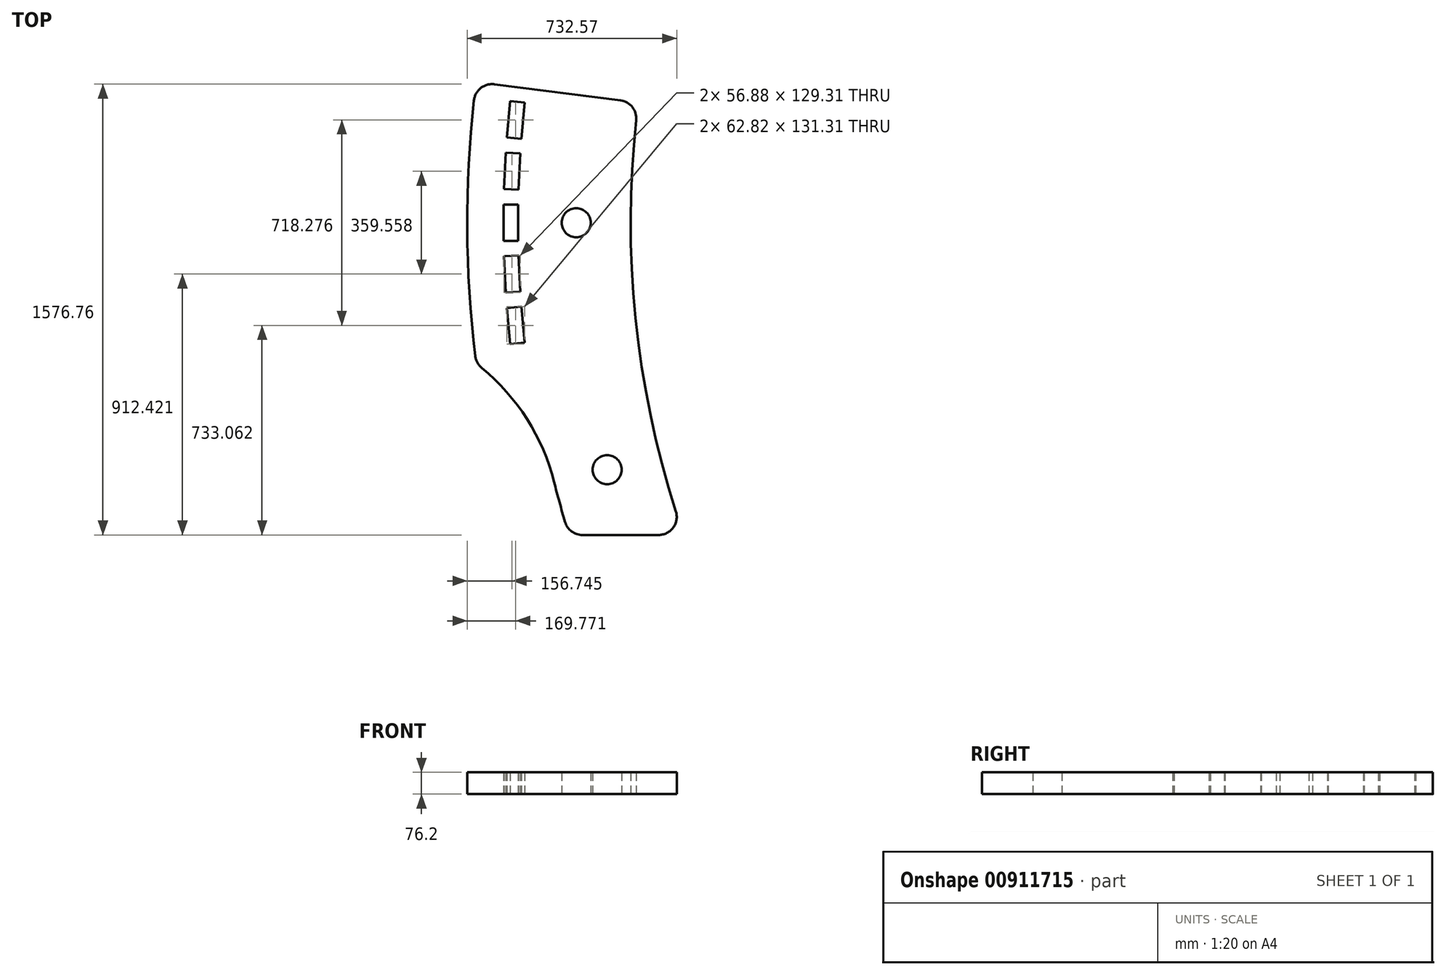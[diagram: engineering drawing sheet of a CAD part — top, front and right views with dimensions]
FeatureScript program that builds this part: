
annotation { "Feature Type Name" : "Feature", "Feature Type Description" : "" }
export const myFeature = defineFeature(function(context is Context, id is Id, definition is map)
    precondition{}
    {
        {
            var Q0;
            Q0=qCreatedBy(makeId("Top.planeOp"),FACE);
            var sketch = newSketch(context, id + "F0", { "sketchPlane" : qUnion([Q0])});
            skLineSegment(sketch, "E0.bottom", {"start": v(-635, -635) * mm, "end": v(635, -635) * mm, "construction": true});
            skLineSegment(sketch, "E0.top", {"start": v(-635, 635) * mm, "end": v(635, 635) * mm, "construction": true});
            skLineSegment(sketch, "E0.left", {"start": v(-635, -635) * mm, "end": v(-635, 635) * mm, "construction": true});
            skLineSegment(sketch, "E0.right", {"start": v(635, -635) * mm, "end": v(635, 635) * mm, "construction": true});
            skPoint(sketch, "E0.middle", {"position": v(0, 0) * mm});
            skPoint(sketch, "E1", {"position": v(0, -635) * mm});
            skLineSegment(sketch, "E2", {"start": v(2487.91, -1226.43) * mm, "end": v(2553.25, -1226.43) * mm});
            skLineSegment(sketch, "E3", {"start": v(2553.25, -1226.43) * mm, "end": v(2589.47, -1126.9) * mm});
            skLineSegment(sketch, "E4", {"start": v(2284.75, -1226.43) * mm, "end": v(2349.36, -1226.43) * mm});
            skLineSegment(sketch, "E5", {"start": v(2349.36, -1226.43) * mm, "end": v(2385.58, -1126.9) * mm});
            skLineSegment(sketch, "E6", {"start": v(2385.58, -1126.9) * mm, "end": v(2451.69, -1126.9) * mm});
            skLineSegment(sketch, "E7", {"start": v(2451.69, -1126.9) * mm, "end": v(2487.91, -1226.43) * mm});
            skLineSegment(sketch, "E8", {"start": v(2081.59, -1226.43) * mm, "end": v(2146.2, -1226.43) * mm});
            skLineSegment(sketch, "E9", {"start": v(2146.2, -1226.43) * mm, "end": v(2182.42, -1126.9) * mm});
            skLineSegment(sketch, "E10", {"start": v(2182.42, -1126.9) * mm, "end": v(2248.52, -1126.9) * mm});
            skLineSegment(sketch, "E11", {"start": v(2248.52, -1126.9) * mm, "end": v(2284.75, -1226.43) * mm});
            skLineSegment(sketch, "E12", {"start": v(1878.43, -1226.43) * mm, "end": v(1943.03, -1226.43) * mm});
            skLineSegment(sketch, "E13", {"start": v(1943.03, -1226.43) * mm, "end": v(1979.26, -1126.9) * mm});
            skLineSegment(sketch, "E14", {"start": v(1979.26, -1126.9) * mm, "end": v(2045.36, -1126.9) * mm});
            skLineSegment(sketch, "E15", {"start": v(2045.36, -1126.9) * mm, "end": v(2081.59, -1226.43) * mm});
            skLineSegment(sketch, "E16", {"start": v(1675.26, -1226.43) * mm, "end": v(1739.87, -1226.43) * mm});
            skLineSegment(sketch, "E17", {"start": v(1739.87, -1226.43) * mm, "end": v(1776.1, -1126.9) * mm});
            skLineSegment(sketch, "E18", {"start": v(1776.1, -1126.9) * mm, "end": v(1842.2, -1126.9) * mm});
            skLineSegment(sketch, "E19", {"start": v(1842.2, -1126.9) * mm, "end": v(1878.43, -1226.43) * mm});
            skLineSegment(sketch, "E20", {"start": v(1472.1, -1226.43) * mm, "end": v(1536.71, -1226.43) * mm});
            skLineSegment(sketch, "E21", {"start": v(1536.71, -1226.43) * mm, "end": v(1572.94, -1126.9) * mm});
            skLineSegment(sketch, "E22", {"start": v(1572.94, -1126.9) * mm, "end": v(1639.04, -1126.9) * mm});
            skLineSegment(sketch, "E23", {"start": v(1639.04, -1126.9) * mm, "end": v(1675.26, -1226.43) * mm});
            skLineSegment(sketch, "E24", {"start": v(1268.94, -1226.43) * mm, "end": v(1333.55, -1226.43) * mm});
            skLineSegment(sketch, "E25", {"start": v(1333.55, -1226.43) * mm, "end": v(1369.77, -1126.9) * mm});
            skLineSegment(sketch, "E26", {"start": v(1369.77, -1126.9) * mm, "end": v(1435.88, -1126.9) * mm});
            skLineSegment(sketch, "E27", {"start": v(1435.88, -1126.9) * mm, "end": v(1472.1, -1226.43) * mm});
            skLineSegment(sketch, "E28", {"start": v(1065.78, -1226.43) * mm, "end": v(1130.39, -1226.43) * mm});
            skLineSegment(sketch, "E29", {"start": v(1130.39, -1226.43) * mm, "end": v(1166.61, -1126.9) * mm});
            skLineSegment(sketch, "E30", {"start": v(1166.61, -1126.9) * mm, "end": v(1232.71, -1126.9) * mm});
            skLineSegment(sketch, "E31", {"start": v(1232.71, -1126.9) * mm, "end": v(1268.94, -1226.43) * mm});
            skLineSegment(sketch, "E32", {"start": v(862.62, -1226.43) * mm, "end": v(927.23, -1226.43) * mm});
            skLineSegment(sketch, "E33", {"start": v(927.23, -1226.43) * mm, "end": v(963.45, -1126.9) * mm});
            skLineSegment(sketch, "E34", {"start": v(963.45, -1126.9) * mm, "end": v(1029.55, -1126.9) * mm});
            skLineSegment(sketch, "E35", {"start": v(1029.55, -1126.9) * mm, "end": v(1065.78, -1226.43) * mm});
            skLineSegment(sketch, "E36", {"start": v(659.45, -1226.43) * mm, "end": v(724.06, -1226.43) * mm});
            skLineSegment(sketch, "E37", {"start": v(724.06, -1226.43) * mm, "end": v(760.29, -1126.9) * mm});
            skLineSegment(sketch, "E38", {"start": v(760.29, -1126.9) * mm, "end": v(826.4, -1126.9) * mm});
            skLineSegment(sketch, "E39", {"start": v(826.4, -1126.9) * mm, "end": v(862.62, -1226.43) * mm});
            skLineSegment(sketch, "E40", {"start": v(456.3, -1226.43) * mm, "end": v(520.9, -1226.43) * mm});
            skLineSegment(sketch, "E41", {"start": v(520.9, -1226.43) * mm, "end": v(557.13, -1126.9) * mm});
            skLineSegment(sketch, "E42", {"start": v(557.13, -1126.9) * mm, "end": v(623.23, -1126.9) * mm});
            skLineSegment(sketch, "E43", {"start": v(623.23, -1126.9) * mm, "end": v(659.45, -1226.43) * mm});
            skLineSegment(sketch, "E44", {"start": v(253.13, -1226.43) * mm, "end": v(317.74, -1226.43) * mm});
            skLineSegment(sketch, "E45", {"start": v(317.74, -1226.43) * mm, "end": v(353.97, -1126.9) * mm});
            skLineSegment(sketch, "E46", {"start": v(353.97, -1126.9) * mm, "end": v(420.07, -1126.9) * mm});
            skLineSegment(sketch, "E47", {"start": v(420.07, -1126.9) * mm, "end": v(456.3, -1226.43) * mm});
            skLineSegment(sketch, "E48", {"start": v(49.97, -1226.43) * mm, "end": v(114.58, -1226.43) * mm});
            skLineSegment(sketch, "E49", {"start": v(114.58, -1226.43) * mm, "end": v(150.8, -1126.9) * mm});
            skLineSegment(sketch, "E50", {"start": v(150.8, -1126.9) * mm, "end": v(216.9, -1126.9) * mm});
            skLineSegment(sketch, "E51", {"start": v(216.9, -1126.9) * mm, "end": v(253.13, -1226.43) * mm});
            skLineSegment(sketch, "E52", {"start": v(-153.2, -1226.43) * mm, "end": v(-88.58, -1226.43) * mm});
            skLineSegment(sketch, "E53", {"start": v(-88.58, -1226.43) * mm, "end": v(-52.36, -1126.9) * mm});
            skLineSegment(sketch, "E54", {"start": v(-52.36, -1126.9) * mm, "end": v(13.74, -1126.9) * mm});
            skLineSegment(sketch, "E55", {"start": v(13.74, -1126.9) * mm, "end": v(49.97, -1226.43) * mm});
            skLineSegment(sketch, "E56", {"start": v(-356.35, -1226.43) * mm, "end": v(-291.75, -1226.43) * mm});
            skLineSegment(sketch, "E57", {"start": v(-291.75, -1226.43) * mm, "end": v(-255.52, -1126.9) * mm});
            skLineSegment(sketch, "E58", {"start": v(-255.52, -1126.9) * mm, "end": v(-189.42, -1126.9) * mm});
            skLineSegment(sketch, "E59", {"start": v(-189.42, -1126.9) * mm, "end": v(-153.2, -1226.43) * mm});
            skLineSegment(sketch, "E60", {"start": v(-559.52, -1226.43) * mm, "end": v(-494.9, -1226.43) * mm});
            skLineSegment(sketch, "E61", {"start": v(-494.9, -1226.43) * mm, "end": v(-458.68, -1126.9) * mm});
            skLineSegment(sketch, "E62", {"start": v(-458.68, -1126.9) * mm, "end": v(-392.58, -1126.9) * mm});
            skLineSegment(sketch, "E63", {"start": v(-392.58, -1126.9) * mm, "end": v(-356.35, -1226.43) * mm});
            skLineSegment(sketch, "E64", {"start": v(-762.68, -1226.43) * mm, "end": v(-698.07, -1226.43) * mm});
            skLineSegment(sketch, "E65", {"start": v(-698.07, -1226.43) * mm, "end": v(-661.84, -1126.9) * mm});
            skLineSegment(sketch, "E66", {"start": v(-661.84, -1126.9) * mm, "end": v(-595.74, -1126.9) * mm});
            skLineSegment(sketch, "E67", {"start": v(-595.74, -1126.9) * mm, "end": v(-559.52, -1226.43) * mm});
            skLineSegment(sketch, "E68", {"start": v(-965.84, -1226.43) * mm, "end": v(-901.23, -1226.43) * mm});
            skLineSegment(sketch, "E69", {"start": v(-901.23, -1226.43) * mm, "end": v(-865, -1126.9) * mm});
            skLineSegment(sketch, "E70", {"start": v(-865, -1126.9) * mm, "end": v(-798.9, -1126.9) * mm});
            skLineSegment(sketch, "E71", {"start": v(-798.9, -1126.9) * mm, "end": v(-762.68, -1226.43) * mm});
            skLineSegment(sketch, "E72", {"start": v(-1169, -1226.43) * mm, "end": v(-1104.4, -1226.43) * mm});
            skLineSegment(sketch, "E73", {"start": v(-1104.4, -1226.43) * mm, "end": v(-1068.17, -1126.9) * mm});
            skLineSegment(sketch, "E74", {"start": v(-1068.17, -1126.9) * mm, "end": v(-1002.06, -1126.9) * mm});
            skLineSegment(sketch, "E75", {"start": v(-1002.06, -1126.9) * mm, "end": v(-965.84, -1226.43) * mm});
            skLineSegment(sketch, "E76", {"start": v(-1372.16, -1226.43) * mm, "end": v(-1307.55, -1226.43) * mm});
            skLineSegment(sketch, "E77", {"start": v(-1307.55, -1226.43) * mm, "end": v(-1271.33, -1126.9) * mm});
            skLineSegment(sketch, "E78", {"start": v(-1271.33, -1126.9) * mm, "end": v(-1205.23, -1126.9) * mm});
            skLineSegment(sketch, "E79", {"start": v(-1205.23, -1126.9) * mm, "end": v(-1169, -1226.43) * mm});
            skLineSegment(sketch, "E80", {"start": v(-1575.32, -1226.43) * mm, "end": v(-1510.72, -1226.43) * mm});
            skLineSegment(sketch, "E81", {"start": v(-1510.72, -1226.43) * mm, "end": v(-1474.5, -1126.9) * mm});
            skLineSegment(sketch, "E82", {"start": v(-1474.5, -1126.9) * mm, "end": v(-1408.39, -1126.9) * mm});
            skLineSegment(sketch, "E83", {"start": v(-1408.39, -1126.9) * mm, "end": v(-1372.16, -1226.43) * mm});
            skLineSegment(sketch, "E84", {"start": v(-1778.49, -1226.43) * mm, "end": v(-1713.88, -1226.43) * mm});
            skLineSegment(sketch, "E85", {"start": v(-1713.88, -1226.43) * mm, "end": v(-1677.65, -1126.9) * mm});
            skLineSegment(sketch, "E86", {"start": v(-1677.65, -1126.9) * mm, "end": v(-1611.55, -1126.9) * mm});
            skLineSegment(sketch, "E87", {"start": v(-1611.55, -1126.9) * mm, "end": v(-1575.32, -1226.43) * mm});
            skLineSegment(sketch, "E88", {"start": v(-1981.65, -1226.43) * mm, "end": v(-1917.04, -1226.43) * mm});
            skLineSegment(sketch, "E89", {"start": v(-1917.04, -1226.43) * mm, "end": v(-1880.81, -1126.9) * mm});
            skLineSegment(sketch, "E90", {"start": v(-1880.81, -1126.9) * mm, "end": v(-1814.71, -1126.9) * mm});
            skLineSegment(sketch, "E91", {"start": v(-1814.71, -1126.9) * mm, "end": v(-1778.49, -1226.43) * mm});
            skLineSegment(sketch, "E92", {"start": v(-2184.8, -1226.43) * mm, "end": v(-2120.2, -1226.43) * mm});
            skLineSegment(sketch, "E93", {"start": v(-2120.2, -1226.43) * mm, "end": v(-2083.98, -1126.9) * mm});
            skLineSegment(sketch, "E94", {"start": v(-2083.98, -1126.9) * mm, "end": v(-2017.87, -1126.9) * mm});
            skLineSegment(sketch, "E95", {"start": v(-2017.87, -1126.9) * mm, "end": v(-1981.65, -1226.43) * mm});
            skLineSegment(sketch, "E96", {"start": v(-2388.2, -1226.43) * mm, "end": v(-2323.36, -1226.43) * mm});
            skLineSegment(sketch, "E97", {"start": v(-2323.36, -1226.43) * mm, "end": v(-2287.14, -1126.9) * mm});
            skLineSegment(sketch, "E98", {"start": v(-2287.14, -1126.9) * mm, "end": v(-2221.04, -1126.9) * mm});
            skLineSegment(sketch, "E99", {"start": v(-2221.04, -1126.9) * mm, "end": v(-2184.8, -1226.43) * mm});
            skLineSegment(sketch, "E100", {"start": v(-2491.46, -1126.9) * mm, "end": v(-2424.43, -1126.9) * mm});
            skLineSegment(sketch, "E101", {"start": v(-2424.43, -1126.9) * mm, "end": v(-2388.2, -1226.43) * mm});
            skCircle(sketch, "E102", {"center": v(-3384.04, -863.6) * mm, "radius": 50.8 * mm});
            skLineSegment(sketch, "E103", {"start": v(-2592.51, -1226.47) * mm, "end": v(-2527.69, -1226.43) * mm});
            skLineSegment(sketch, "E104", {"start": v(-2527.69, -1226.43) * mm, "end": v(-2491.46, -1126.9) * mm});
            skLineSegment(sketch, "E105", {"start": v(-2629.3, -1126.9) * mm, "end": v(-2592.51, -1226.47) * mm});
            skLineSegment(sketch, "E106", {"start": v(-2696.33, -1126.9) * mm, "end": v(-2629.3, -1126.9) * mm});
            skLineSegment(sketch, "E107", {"start": v(-2733.1, -1226.43) * mm, "end": v(-2696.33, -1126.9) * mm});
            skLineSegment(sketch, "E108", {"start": v(2691.8, -1226.43) * mm, "end": v(2757.13, -1226.43) * mm});
            skLineSegment(sketch, "E109", {"start": v(2757.13, -1226.43) * mm, "end": v(2794, -1126.75) * mm});
            skLineSegment(sketch, "E110", {"start": v(2589.47, -1126.9) * mm, "end": v(2655.57, -1126.9) * mm});
            skLineSegment(sketch, "E111", {"start": v(2655.57, -1126.9) * mm, "end": v(2691.8, -1226.43) * mm});
            skLineSegment(sketch, "E112", {"start": v(-2794.02, -1226.47) * mm, "end": v(-2733.1, -1226.43) * mm});
            skCircle(sketch, "E113", {"center": v(-2980.94, -863.6) * mm, "radius": 76.2 * mm});
            skCircle(sketch, "E114", {"center": v(3463.58, -863.6) * mm, "radius": 76.2 * mm});
            skLineSegment(sketch, "E115", {"start": v(-2980.94, -787.4) * mm, "end": v(3463.58, -787.4) * mm});
            skLineSegment(sketch, "E116", {"start": v(3463.58, -939.8) * mm, "end": v(-2980.94, -939.8) * mm});
            skLineSegment(sketch, "E117.bottom", {"start": v(-2794, -635) * mm, "end": v(2794, -635) * mm});
            skLineSegment(sketch, "E117.top", {"start": v(-2794, -1176.6) * mm, "end": v(3692.18, -1176.6) * mm, "construction": true});
            skLineSegment(sketch, "E117.left", {"start": v(-2794, -635) * mm, "end": v(-2794, -1176.6) * mm});
            skLineSegment(sketch, "E118", {"start": v(-2794.02, -1226.47) * mm, "end": v(-2794, -1176.6) * mm});
            skLineSegment(sketch, "E119.bottom", {"start": v(-2794, -635) * mm, "end": v(-4256.94, -635) * mm});
            skLineSegment(sketch, "E119.top", {"start": v(-2794, -1092.2) * mm, "end": v(-4256.94, -1092.2) * mm});
            skLineSegment(sketch, "E119.left", {"start": v(-2794, -635) * mm, "end": v(-2794, -1092.2) * mm});
            skLineSegment(sketch, "E119.right", {"start": v(-4256.94, -635) * mm, "end": v(-4256.94, -1092.2) * mm});
            skLineSegment(sketch, "E120.bottom", {"start": v(2794, -635) * mm, "end": v(3692.18, -635) * mm});
            skLineSegment(sketch, "E120.right", {"start": v(3692.18, -635) * mm, "end": v(3692.18, -1238.28) * mm});
            skPoint(sketch, "E121", {"position": v(-3803.14, -635) * mm});
            skPoint(sketch, "E122", {"position": v(3237.88, -635) * mm});
            skLineSegment(sketch, "E123", {"start": v(2896.33, -1226.28) * mm, "end": v(2961.66, -1226.28) * mm});
            skLineSegment(sketch, "E124", {"start": v(2961.66, -1226.28) * mm, "end": v(2998.53, -1126.6) * mm});
            skLineSegment(sketch, "E125", {"start": v(2794, -1126.75) * mm, "end": v(2860.1, -1126.75) * mm});
            skLineSegment(sketch, "E126", {"start": v(2860.1, -1126.75) * mm, "end": v(2896.33, -1226.28) * mm});
            skLineSegment(sketch, "E127", {"start": v(3100.86, -1226.14) * mm, "end": v(3166.2, -1226.14) * mm});
            skLineSegment(sketch, "E128", {"start": v(3166.2, -1226.14) * mm, "end": v(3203.06, -1126.46) * mm});
            skLineSegment(sketch, "E129", {"start": v(2998.53, -1126.6) * mm, "end": v(3064.63, -1126.6) * mm});
            skLineSegment(sketch, "E130", {"start": v(3064.63, -1126.6) * mm, "end": v(3100.86, -1226.14) * mm});
            skLineSegment(sketch, "E131", {"start": v(3305.39, -1226) * mm, "end": v(3370.72, -1226) * mm});
            skLineSegment(sketch, "E132", {"start": v(3370.72, -1226) * mm, "end": v(3407.59, -1126.32) * mm});
            skLineSegment(sketch, "E133", {"start": v(3203.06, -1126.46) * mm, "end": v(3269.16, -1126.46) * mm});
            skLineSegment(sketch, "E134", {"start": v(3269.16, -1126.46) * mm, "end": v(3305.39, -1226) * mm});
            skLineSegment(sketch, "E135", {"start": v(3509.7, -1226.43) * mm, "end": v(3575.03, -1226.43) * mm});
            skLineSegment(sketch, "E136", {"start": v(3575.03, -1226.43) * mm, "end": v(3611.9, -1126.75) * mm});
            skLineSegment(sketch, "E137", {"start": v(3407.37, -1126.9) * mm, "end": v(3473.47, -1126.9) * mm});
            skLineSegment(sketch, "E138", {"start": v(3473.47, -1126.9) * mm, "end": v(3509.7, -1226.43) * mm});
            skLineSegment(sketch, "E139", {"start": v(3611.9, -1126.75) * mm, "end": v(3692.18, -1126.75) * mm});
            skPoint(sketch, "E140", {"position": v(3692.18, -1176.6) * mm});
            skPoint(sketch, "E140.positionSnap0", {"position": v(3593.47, -1176.6) * mm});
            skLineSegment(sketch, "E141.bottom", {"start": v(-3107.94, -635) * mm, "end": v(-2853.94, -635) * mm});
            skLineSegment(sketch, "E141.top", {"start": v(-3107.94, -254) * mm, "end": v(-2853.94, -254) * mm});
            skLineSegment(sketch, "E141.left", {"start": v(-3107.94, -635) * mm, "end": v(-3107.94, -254) * mm});
            skLineSegment(sketch, "E141.right", {"start": v(-2853.94, -635) * mm, "end": v(-2853.94, -254) * mm});
            skPoint(sketch, "E142", {"position": v(-2980.94, -635) * mm});
            skCircle(sketch, "E143", {"center": v(0, 0) * mm, "radius": 3302 * mm});
            skCircle(sketch, "E144", {"center": v(0, 0) * mm, "radius": 3683 * mm});
            skCircle(sketch, "E145", {"center": v(0, 0) * mm, "radius": 3492.5 * mm, "construction": true});
            skLineSegment(sketch, "E146", {"start": v(-2980.94, -863.6) * mm, "end": v(-3692.14, -863.6) * mm, "construction": true});
            skLineSegment(sketch, "E147", {"start": v(0, 0) * mm, "end": v(-3873.5, 0) * mm, "construction": true});
            skCircle(sketch, "E148", {"center": v(-3492.5, 0) * mm, "radius": 50.8 * mm});
            skLineSegment(sketch, "E149", {"start": v(0, 0) * mm, "end": v(-3842.1, 492.18) * mm});
            skCircle(sketch, "E150", {"center": v(0, 0) * mm, "radius": 3873.5 * mm});
            skLineSegment(sketch, "E151.bottom", {"start": v(-3746.5, -63.5) * mm, "end": v(-3695.7, -63.5) * mm});
            skLineSegment(sketch, "E151.top", {"start": v(-3746.5, 63.5) * mm, "end": v(-3695.7, 63.5) * mm});
            skLineSegment(sketch, "E151.left", {"start": v(-3746.5, -63.5) * mm, "end": v(-3746.5, 63.5) * mm});
            skLineSegment(sketch, "E151.right", {"start": v(-3695.7, -63.5) * mm, "end": v(-3695.7, 63.5) * mm});
            skPoint(sketch, "E151.middle", {"position": v(-3721.1, 0) * mm});
            skLineSegment(sketch, "E152.1.0", {"start": v(-3739.06, -244.43) * mm, "end": v(-3688.32, -241.98) * mm});
            skLineSegment(sketch, "E152.1.1", {"start": v(-3688.32, -241.98) * mm, "end": v(-3694.45, -115.13) * mm});
            skLineSegment(sketch, "E152.1.2", {"start": v(-3745.2, -117.58) * mm, "end": v(-3694.45, -115.13) * mm});
            skLineSegment(sketch, "E152.1.3", {"start": v(-3739.06, -244.43) * mm, "end": v(-3745.2, -117.58) * mm});
            skLineSegment(sketch, "E152.2.0", {"start": v(-3722.88, -424.8) * mm, "end": v(-3672.32, -419.9) * mm});
            skLineSegment(sketch, "E152.2.1", {"start": v(-3672.32, -419.9) * mm, "end": v(-3684.58, -293.48) * mm});
            skLineSegment(sketch, "E152.2.2", {"start": v(-3735.14, -298.39) * mm, "end": v(-3684.58, -293.48) * mm});
            skLineSegment(sketch, "E152.2.3", {"start": v(-3722.88, -424.8) * mm, "end": v(-3735.14, -298.39) * mm});
            skLineSegment(sketch, "E152.3.0", {"start": v(-3698.01, -604.16) * mm, "end": v(-3647.74, -596.82) * mm});
            skLineSegment(sketch, "E152.3.1", {"start": v(-3647.74, -596.82) * mm, "end": v(-3666.1, -471.15) * mm});
            skLineSegment(sketch, "E152.3.2", {"start": v(-3716.36, -478.5) * mm, "end": v(-3666.1, -471.15) * mm});
            skLineSegment(sketch, "E152.3.3", {"start": v(-3698.01, -604.16) * mm, "end": v(-3716.36, -478.5) * mm});
            skLineSegment(sketch, "E152.4.0", {"start": v(-3664.5, -782.12) * mm, "end": v(-3614.65, -772.36) * mm});
            skLineSegment(sketch, "E152.4.1", {"start": v(-3614.65, -772.36) * mm, "end": v(-3639.05, -647.73) * mm});
            skLineSegment(sketch, "E152.4.2", {"start": v(-3688.9, -657.49) * mm, "end": v(-3639.05, -647.73) * mm});
            skLineSegment(sketch, "E152.4.3", {"start": v(-3664.5, -782.12) * mm, "end": v(-3688.9, -657.49) * mm});
            skLineSegment(sketch, "E152.5.0", {"start": v(-3622.44, -958.25) * mm, "end": v(-3573.11, -946.1) * mm});
            skLineSegment(sketch, "E152.5.1", {"start": v(-3573.11, -946.1) * mm, "end": v(-3603.5, -822.78) * mm});
            skLineSegment(sketch, "E152.5.2", {"start": v(-3652.83, -834.94) * mm, "end": v(-3603.5, -822.78) * mm});
            skLineSegment(sketch, "E152.5.3", {"start": v(-3622.44, -958.25) * mm, "end": v(-3652.83, -834.94) * mm});
            skLineSegment(sketch, "E152.6.0", {"start": v(-3571.91, -1132.14) * mm, "end": v(-3523.23, -1117.62) * mm});
            skLineSegment(sketch, "E152.6.1", {"start": v(-3523.23, -1117.62) * mm, "end": v(-3559.55, -995.92) * mm});
            skLineSegment(sketch, "E152.6.2", {"start": v(-3608.23, -1010.45) * mm, "end": v(-3559.55, -995.92) * mm});
            skLineSegment(sketch, "E152.6.3", {"start": v(-3571.91, -1132.14) * mm, "end": v(-3608.23, -1010.45) * mm});
            skLineSegment(sketch, "E152.7.0", {"start": v(-3513.04, -1303.4) * mm, "end": v(-3465.12, -1286.53) * mm});
            skLineSegment(sketch, "E152.7.1", {"start": v(-3465.12, -1286.53) * mm, "end": v(-3507.27, -1166.73) * mm});
            skLineSegment(sketch, "E152.7.2", {"start": v(-3555.2, -1183.6) * mm, "end": v(-3507.27, -1166.73) * mm});
            skLineSegment(sketch, "E152.7.3", {"start": v(-3513.04, -1303.4) * mm, "end": v(-3555.2, -1183.6) * mm});
            skLineSegment(sketch, "E152.8.0", {"start": v(-3445.97, -1471.6) * mm, "end": v(-3398.92, -1452.44) * mm});
            skLineSegment(sketch, "E152.8.1", {"start": v(-3398.92, -1452.44) * mm, "end": v(-3446.8, -1334.82) * mm});
            skLineSegment(sketch, "E152.8.2", {"start": v(-3493.86, -1353.97) * mm, "end": v(-3446.8, -1334.82) * mm});
            skLineSegment(sketch, "E152.8.3", {"start": v(-3445.97, -1471.6) * mm, "end": v(-3493.86, -1353.97) * mm});
            skLineSegment(sketch, "E152.9.0", {"start": v(-3370.85, -1636.37) * mm, "end": v(-3324.78, -1614.96) * mm});
            skLineSegment(sketch, "E152.9.1", {"start": v(-3324.78, -1614.96) * mm, "end": v(-3378.3, -1499.79) * mm});
            skLineSegment(sketch, "E152.9.2", {"start": v(-3424.36, -1521.2) * mm, "end": v(-3378.3, -1499.79) * mm});
            skLineSegment(sketch, "E152.9.3", {"start": v(-3370.85, -1636.37) * mm, "end": v(-3424.36, -1521.2) * mm});
            skLineSegment(sketch, "E152.10.0", {"start": v(-3287.85, -1797.31) * mm, "end": v(-3242.87, -1773.7) * mm});
            skLineSegment(sketch, "E152.10.1", {"start": v(-3242.87, -1773.7) * mm, "end": v(-3301.89, -1661.25) * mm});
            skLineSegment(sketch, "E152.10.2", {"start": v(-3346.87, -1684.86) * mm, "end": v(-3301.89, -1661.25) * mm});
            skLineSegment(sketch, "E152.10.3", {"start": v(-3287.85, -1797.31) * mm, "end": v(-3346.87, -1684.86) * mm});
            skLineSegment(sketch, "E152.11.0", {"start": v(-3197.18, -1954.06) * mm, "end": v(-3153.39, -1928.3) * mm});
            skLineSegment(sketch, "E152.11.1", {"start": v(-3153.39, -1928.3) * mm, "end": v(-3217.77, -1818.84) * mm});
            skLineSegment(sketch, "E152.11.2", {"start": v(-3261.56, -1844.6) * mm, "end": v(-3217.77, -1818.84) * mm});
            skLineSegment(sketch, "E152.11.3", {"start": v(-3197.18, -1954.06) * mm, "end": v(-3261.56, -1844.6) * mm});
            skLineSegment(sketch, "E152.12.0", {"start": v(-3099.04, -2106.24) * mm, "end": v(-3056.54, -2078.4) * mm});
            skLineSegment(sketch, "E152.12.1", {"start": v(-3056.54, -2078.4) * mm, "end": v(-3126.14, -1972.17) * mm});
            skLineSegment(sketch, "E152.12.2", {"start": v(-3168.63, -2000.01) * mm, "end": v(-3126.14, -1972.17) * mm});
            skLineSegment(sketch, "E152.12.3", {"start": v(-3099.04, -2106.24) * mm, "end": v(-3168.63, -2000.01) * mm});
            skLineSegment(sketch, "E153", {"start": v(0, 0) * mm, "end": v(-3842.1, -492.18) * mm});
            skLineSegment(sketch, "E154.1.13.0", {"start": v(-2993.66, -2253.51) * mm, "end": v(-2952.56, -2223.65) * mm});
            skLineSegment(sketch, "E154.3.13.0", {"start": v(-2952.56, -2223.65) * mm, "end": v(-3027.2, -2120.9) * mm});
            skLineSegment(sketch, "E154.6.13.0", {"start": v(-3068.3, -2150.76) * mm, "end": v(-3027.2, -2120.9) * mm});
            skLineSegment(sketch, "E154.9.13.0", {"start": v(-2993.66, -2253.51) * mm, "end": v(-3068.3, -2150.76) * mm});
            skLineSegment(sketch, "E154.1.14.0", {"start": v(-2881.29, -2395.51) * mm, "end": v(-2841.68, -2363.7) * mm});
            skLineSegment(sketch, "E154.3.14.0", {"start": v(-2841.68, -2363.7) * mm, "end": v(-2921.2, -2264.68) * mm});
            skLineSegment(sketch, "E154.6.14.0", {"start": v(-2960.81, -2296.5) * mm, "end": v(-2921.2, -2264.68) * mm});
            skLineSegment(sketch, "E154.9.14.0", {"start": v(-2881.29, -2395.51) * mm, "end": v(-2960.81, -2296.5) * mm});
            skLineSegment(sketch, "E154.1.15.0", {"start": v(-2762.19, -2531.92) * mm, "end": v(-2724.16, -2498.23) * mm});
            skLineSegment(sketch, "E154.3.15.0", {"start": v(-2724.16, -2498.23) * mm, "end": v(-2808.38, -2403.17) * mm});
            skLineSegment(sketch, "E154.6.15.0", {"start": v(-2846.4, -2436.86) * mm, "end": v(-2808.38, -2403.17) * mm});
            skLineSegment(sketch, "E154.9.15.0", {"start": v(-2762.19, -2531.92) * mm, "end": v(-2846.4, -2436.86) * mm});
            skLineSegment(sketch, "E154.1.16.0", {"start": v(-2636.64, -2662.41) * mm, "end": v(-2600.28, -2626.93) * mm});
            skLineSegment(sketch, "E154.3.16.0", {"start": v(-2600.28, -2626.93) * mm, "end": v(-2689, -2536.05) * mm});
            skLineSegment(sketch, "E154.6.16.0", {"start": v(-2725.35, -2571.53) * mm, "end": v(-2689, -2536.05) * mm});
            skLineSegment(sketch, "E154.9.16.0", {"start": v(-2636.64, -2662.41) * mm, "end": v(-2725.35, -2571.53) * mm});
            skLineSegment(sketch, "E154.1.17.0", {"start": v(-2504.93, -2786.69) * mm, "end": v(-2470.33, -2749.49) * mm});
            skLineSegment(sketch, "E154.3.17.0", {"start": v(-2470.33, -2749.49) * mm, "end": v(-2563.33, -2663) * mm});
            skLineSegment(sketch, "E154.6.17.0", {"start": v(-2597.92, -2700.2) * mm, "end": v(-2563.33, -2663) * mm});
            skLineSegment(sketch, "E154.9.17.0", {"start": v(-2504.93, -2786.69) * mm, "end": v(-2597.92, -2700.2) * mm});
            skLineSegment(sketch, "E154.1.18.0", {"start": v(-2367.37, -2904.46) * mm, "end": v(-2334.6, -2865.63) * mm});
            skLineSegment(sketch, "E154.3.18.0", {"start": v(-2334.6, -2865.63) * mm, "end": v(-2431.68, -2783.73) * mm});
            skLineSegment(sketch, "E154.6.18.0", {"start": v(-2464.44, -2822.56) * mm, "end": v(-2431.68, -2783.73) * mm});
            skLineSegment(sketch, "E154.9.18.0", {"start": v(-2367.37, -2904.46) * mm, "end": v(-2464.44, -2822.56) * mm});
            skLineSegment(sketch, "E154.1.19.0", {"start": v(-2224.28, -3015.44) * mm, "end": v(-2193.43, -2975.08) * mm});
            skLineSegment(sketch, "E154.3.19.0", {"start": v(-2193.43, -2975.08) * mm, "end": v(-2294.35, -2897.97) * mm});
            skLineSegment(sketch, "E154.6.19.0", {"start": v(-2325.2, -2938.33) * mm, "end": v(-2294.35, -2897.97) * mm});
            skLineSegment(sketch, "E154.9.19.0", {"start": v(-2224.28, -3015.44) * mm, "end": v(-2325.2, -2938.33) * mm});
            skLineSegment(sketch, "E154.1.20.0", {"start": v(-2076, -3119.38) * mm, "end": v(-2047.14, -3077.57) * mm});
            skLineSegment(sketch, "E154.3.20.0", {"start": v(-2047.14, -3077.57) * mm, "end": v(-2151.66, -3005.43) * mm});
            skLineSegment(sketch, "E154.6.20.0", {"start": v(-2180.51, -3047.24) * mm, "end": v(-2151.66, -3005.43) * mm});
            skLineSegment(sketch, "E154.9.20.0", {"start": v(-2076, -3119.38) * mm, "end": v(-2180.51, -3047.24) * mm});
            skLineSegment(sketch, "E154.1.21.0", {"start": v(-1922.86, -3216.04) * mm, "end": v(-1896.06, -3172.88) * mm});
            skLineSegment(sketch, "E154.3.21.0", {"start": v(-1896.06, -3172.88) * mm, "end": v(-2003.94, -3105.87) * mm});
            skLineSegment(sketch, "E154.6.21.0", {"start": v(-2030.75, -3149.03) * mm, "end": v(-2003.94, -3105.87) * mm});
            skLineSegment(sketch, "E154.9.21.0", {"start": v(-1922.86, -3216.04) * mm, "end": v(-2030.75, -3149.03) * mm});
            skLineSegment(sketch, "E154.1.22.0", {"start": v(-1765.24, -3305.18) * mm, "end": v(-1740.55, -3260.78) * mm});
            skLineSegment(sketch, "E154.3.22.0", {"start": v(-1740.55, -3260.78) * mm, "end": v(-1851.55, -3199.06) * mm});
            skLineSegment(sketch, "E154.6.22.0", {"start": v(-1876.23, -3243.46) * mm, "end": v(-1851.55, -3199.06) * mm});
            skLineSegment(sketch, "E154.9.22.0", {"start": v(-1765.24, -3305.18) * mm, "end": v(-1876.23, -3243.46) * mm});
            skLineSegment(sketch, "E154.1.23.0", {"start": v(-1603.5, -3386.6) * mm, "end": v(-1580.98, -3341.07) * mm});
            skLineSegment(sketch, "E154.3.23.0", {"start": v(-1580.98, -3341.07) * mm, "end": v(-1694.83, -3284.78) * mm});
            skLineSegment(sketch, "E154.6.23.0", {"start": v(-1717.34, -3330.32) * mm, "end": v(-1694.83, -3284.78) * mm});
            skLineSegment(sketch, "E154.9.23.0", {"start": v(-1603.5, -3386.6) * mm, "end": v(-1717.34, -3330.32) * mm});
            skLineSegment(sketch, "E154.1.24.0", {"start": v(-1438, -3460.12) * mm, "end": v(-1417.72, -3413.55) * mm});
            skLineSegment(sketch, "E154.3.24.0", {"start": v(-1417.72, -3413.55) * mm, "end": v(-1534.15, -3362.83) * mm});
            skLineSegment(sketch, "E154.6.24.0", {"start": v(-1554.44, -3409.4) * mm, "end": v(-1534.15, -3362.83) * mm});
            skLineSegment(sketch, "E154.9.24.0", {"start": v(-1438, -3460.12) * mm, "end": v(-1554.44, -3409.4) * mm});
            skLineSegment(sketch, "E154.1.25.0", {"start": v(-1269.15, -3525.56) * mm, "end": v(-1251.14, -3478.06) * mm});
            skLineSegment(sketch, "E154.3.25.0", {"start": v(-1251.14, -3478.06) * mm, "end": v(-1369.89, -3433.02) * mm});
            skLineSegment(sketch, "E154.6.25.0", {"start": v(-1387.9, -3480.52) * mm, "end": v(-1369.89, -3433.02) * mm});
            skLineSegment(sketch, "E154.9.25.0", {"start": v(-1269.15, -3525.56) * mm, "end": v(-1387.9, -3480.52) * mm});
            skLineSegment(sketch, "E154.1.26.0", {"start": v(-1097.34, -3582.76) * mm, "end": v(-1081.64, -3534.44) * mm});
            skLineSegment(sketch, "E154.3.26.0", {"start": v(-1081.64, -3534.44) * mm, "end": v(-1202.43, -3495.2) * mm});
            skLineSegment(sketch, "E154.6.26.0", {"start": v(-1218.12, -3543.51) * mm, "end": v(-1202.43, -3495.2) * mm});
            skLineSegment(sketch, "E154.9.26.0", {"start": v(-1097.34, -3582.76) * mm, "end": v(-1218.12, -3543.51) * mm});
            skLineSegment(sketch, "E154.1.27.0", {"start": v(-922.96, -3631.59) * mm, "end": v(-909.62, -3582.57) * mm});
            skLineSegment(sketch, "E154.3.27.0", {"start": v(-909.62, -3582.57) * mm, "end": v(-1032.16, -3549.2) * mm});
            skLineSegment(sketch, "E154.6.27.0", {"start": v(-1045.5, -3598.22) * mm, "end": v(-1032.16, -3549.2) * mm});
            skLineSegment(sketch, "E154.9.27.0", {"start": v(-922.96, -3631.59) * mm, "end": v(-1045.5, -3598.22) * mm});
            skLineSegment(sketch, "E154.1.28.0", {"start": v(-746.43, -3671.94) * mm, "end": v(-735.47, -3622.34) * mm});
            skLineSegment(sketch, "E154.3.28.0", {"start": v(-735.47, -3622.34) * mm, "end": v(-859.48, -3594.93) * mm});
            skLineSegment(sketch, "E154.6.28.0", {"start": v(-870.44, -3644.53) * mm, "end": v(-859.48, -3594.93) * mm});
            skLineSegment(sketch, "E154.9.28.0", {"start": v(-746.43, -3671.94) * mm, "end": v(-870.44, -3644.53) * mm});
            skLineSegment(sketch, "E154.1.29.0", {"start": v(-568.16, -3703.71) * mm, "end": v(-559.6, -3653.64) * mm});
            skLineSegment(sketch, "E154.3.29.0", {"start": v(-559.6, -3653.64) * mm, "end": v(-684.8, -3632.26) * mm});
            skLineSegment(sketch, "E154.6.29.0", {"start": v(-693.34, -3682.33) * mm, "end": v(-684.8, -3632.26) * mm});
            skLineSegment(sketch, "E154.9.29.0", {"start": v(-568.16, -3703.71) * mm, "end": v(-693.34, -3682.33) * mm});
            skLineSegment(sketch, "E154.1.30.0", {"start": v(-388.55, -3726.84) * mm, "end": v(-382.43, -3676.4) * mm});
            skLineSegment(sketch, "E154.3.30.0", {"start": v(-382.43, -3676.4) * mm, "end": v(-508.5, -3661.1) * mm});
            skLineSegment(sketch, "E154.6.30.0", {"start": v(-514.63, -3711.53) * mm, "end": v(-508.5, -3661.1) * mm});
            skLineSegment(sketch, "E154.9.30.0", {"start": v(-388.55, -3726.84) * mm, "end": v(-514.63, -3711.53) * mm});
            skLineSegment(sketch, "E154.1.31.0", {"start": v(-208.04, -3741.26) * mm, "end": v(-204.36, -3690.6) * mm});
            skLineSegment(sketch, "E154.3.31.0", {"start": v(-204.36, -3690.6) * mm, "end": v(-331.03, -3681.4) * mm});
            skLineSegment(sketch, "E154.6.31.0", {"start": v(-334.71, -3732.06) * mm, "end": v(-331.03, -3681.4) * mm});
            skLineSegment(sketch, "E154.9.31.0", {"start": v(-208.04, -3741.26) * mm, "end": v(-334.71, -3732.06) * mm});
            skLineSegment(sketch, "E154.1.32.0", {"start": v(-27.05, -3746.94) * mm, "end": v(-25.82, -3696.16) * mm});
            skLineSegment(sketch, "E154.3.32.0", {"start": v(-25.82, -3696.16) * mm, "end": v(-152.78, -3693.09) * mm});
            skLineSegment(sketch, "E154.6.32.0", {"start": v(-154.01, -3743.87) * mm, "end": v(-152.78, -3693.09) * mm});
            skLineSegment(sketch, "E154.9.32.0", {"start": v(-27.05, -3746.94) * mm, "end": v(-154.01, -3743.87) * mm});
            skLineSegment(sketch, "E154.1.33.0", {"start": v(154.01, -3743.87) * mm, "end": v(152.78, -3693.09) * mm});
            skLineSegment(sketch, "E154.3.33.0", {"start": v(152.78, -3693.09) * mm, "end": v(25.82, -3696.16) * mm});
            skLineSegment(sketch, "E154.6.33.0", {"start": v(27.05, -3746.94) * mm, "end": v(25.82, -3696.16) * mm});
            skLineSegment(sketch, "E154.9.33.0", {"start": v(154.01, -3743.87) * mm, "end": v(27.05, -3746.94) * mm});
            skLineSegment(sketch, "E154.1.34.0", {"start": v(334.71, -3732.06) * mm, "end": v(331.03, -3681.4) * mm});
            skLineSegment(sketch, "E154.3.34.0", {"start": v(331.03, -3681.4) * mm, "end": v(204.36, -3690.6) * mm});
            skLineSegment(sketch, "E154.6.34.0", {"start": v(208.04, -3741.26) * mm, "end": v(204.36, -3690.6) * mm});
            skLineSegment(sketch, "E154.9.34.0", {"start": v(334.71, -3732.06) * mm, "end": v(208.04, -3741.26) * mm});
            skLineSegment(sketch, "E154.1.35.0", {"start": v(514.63, -3711.53) * mm, "end": v(508.5, -3661.1) * mm});
            skLineSegment(sketch, "E154.3.35.0", {"start": v(508.5, -3661.1) * mm, "end": v(382.43, -3676.4) * mm});
            skLineSegment(sketch, "E154.6.35.0", {"start": v(388.55, -3726.84) * mm, "end": v(382.43, -3676.4) * mm});
            skLineSegment(sketch, "E154.9.35.0", {"start": v(514.63, -3711.53) * mm, "end": v(388.55, -3726.84) * mm});
            skLineSegment(sketch, "E154.1.36.0", {"start": v(693.34, -3682.33) * mm, "end": v(684.8, -3632.26) * mm});
            skLineSegment(sketch, "E154.3.36.0", {"start": v(684.8, -3632.26) * mm, "end": v(559.6, -3653.64) * mm});
            skLineSegment(sketch, "E154.6.36.0", {"start": v(568.16, -3703.71) * mm, "end": v(559.6, -3653.64) * mm});
            skLineSegment(sketch, "E154.9.36.0", {"start": v(693.34, -3682.33) * mm, "end": v(568.16, -3703.71) * mm});
            skLineSegment(sketch, "E154.1.37.0", {"start": v(870.44, -3644.53) * mm, "end": v(859.48, -3594.93) * mm});
            skLineSegment(sketch, "E154.3.37.0", {"start": v(859.48, -3594.93) * mm, "end": v(735.47, -3622.34) * mm});
            skLineSegment(sketch, "E154.6.37.0", {"start": v(746.43, -3671.94) * mm, "end": v(735.47, -3622.34) * mm});
            skLineSegment(sketch, "E154.9.37.0", {"start": v(870.44, -3644.53) * mm, "end": v(746.43, -3671.94) * mm});
            skLineSegment(sketch, "E154.1.38.0", {"start": v(1045.5, -3598.22) * mm, "end": v(1032.16, -3549.2) * mm});
            skLineSegment(sketch, "E154.3.38.0", {"start": v(1032.16, -3549.2) * mm, "end": v(909.62, -3582.57) * mm});
            skLineSegment(sketch, "E154.6.38.0", {"start": v(922.96, -3631.59) * mm, "end": v(909.62, -3582.57) * mm});
            skLineSegment(sketch, "E154.9.38.0", {"start": v(1045.5, -3598.22) * mm, "end": v(922.96, -3631.59) * mm});
            skLineSegment(sketch, "E154.1.39.0", {"start": v(1218.12, -3543.51) * mm, "end": v(1202.43, -3495.2) * mm});
            skLineSegment(sketch, "E154.3.39.0", {"start": v(1202.43, -3495.2) * mm, "end": v(1081.64, -3534.44) * mm});
            skLineSegment(sketch, "E154.6.39.0", {"start": v(1097.34, -3582.76) * mm, "end": v(1081.64, -3534.44) * mm});
            skLineSegment(sketch, "E154.9.39.0", {"start": v(1218.12, -3543.51) * mm, "end": v(1097.34, -3582.76) * mm});
            skLineSegment(sketch, "E154.1.40.0", {"start": v(1387.9, -3480.52) * mm, "end": v(1369.89, -3433.02) * mm});
            skLineSegment(sketch, "E154.3.40.0", {"start": v(1369.89, -3433.02) * mm, "end": v(1251.14, -3478.06) * mm});
            skLineSegment(sketch, "E154.6.40.0", {"start": v(1269.15, -3525.56) * mm, "end": v(1251.14, -3478.06) * mm});
            skLineSegment(sketch, "E154.9.40.0", {"start": v(1387.9, -3480.52) * mm, "end": v(1269.15, -3525.56) * mm});
            skLineSegment(sketch, "E154.1.41.0", {"start": v(1554.44, -3409.4) * mm, "end": v(1534.15, -3362.83) * mm});
            skLineSegment(sketch, "E154.3.41.0", {"start": v(1534.15, -3362.83) * mm, "end": v(1417.72, -3413.55) * mm});
            skLineSegment(sketch, "E154.6.41.0", {"start": v(1438, -3460.12) * mm, "end": v(1417.72, -3413.55) * mm});
            skLineSegment(sketch, "E154.9.41.0", {"start": v(1554.44, -3409.4) * mm, "end": v(1438, -3460.12) * mm});
            skLineSegment(sketch, "E154.1.42.0", {"start": v(1717.34, -3330.32) * mm, "end": v(1694.83, -3284.78) * mm});
            skLineSegment(sketch, "E154.3.42.0", {"start": v(1694.83, -3284.78) * mm, "end": v(1580.98, -3341.07) * mm});
            skLineSegment(sketch, "E154.6.42.0", {"start": v(1603.5, -3386.6) * mm, "end": v(1580.98, -3341.07) * mm});
            skLineSegment(sketch, "E154.9.42.0", {"start": v(1717.34, -3330.32) * mm, "end": v(1603.5, -3386.6) * mm});
            skLineSegment(sketch, "E154.1.43.0", {"start": v(1876.23, -3243.46) * mm, "end": v(1851.55, -3199.06) * mm});
            skLineSegment(sketch, "E154.3.43.0", {"start": v(1851.55, -3199.06) * mm, "end": v(1740.55, -3260.78) * mm});
            skLineSegment(sketch, "E154.6.43.0", {"start": v(1765.24, -3305.18) * mm, "end": v(1740.55, -3260.78) * mm});
            skLineSegment(sketch, "E154.9.43.0", {"start": v(1876.23, -3243.46) * mm, "end": v(1765.24, -3305.18) * mm});
            skLineSegment(sketch, "E154.1.44.0", {"start": v(2030.75, -3149.03) * mm, "end": v(2003.94, -3105.87) * mm});
            skLineSegment(sketch, "E154.3.44.0", {"start": v(2003.94, -3105.87) * mm, "end": v(1896.06, -3172.88) * mm});
            skLineSegment(sketch, "E154.6.44.0", {"start": v(1922.86, -3216.04) * mm, "end": v(1896.06, -3172.88) * mm});
            skLineSegment(sketch, "E154.9.44.0", {"start": v(2030.75, -3149.03) * mm, "end": v(1922.86, -3216.04) * mm});
            skLineSegment(sketch, "E154.1.45.0", {"start": v(2180.51, -3047.24) * mm, "end": v(2151.66, -3005.43) * mm});
            skLineSegment(sketch, "E154.3.45.0", {"start": v(2151.66, -3005.43) * mm, "end": v(2047.14, -3077.57) * mm});
            skLineSegment(sketch, "E154.6.45.0", {"start": v(2076, -3119.38) * mm, "end": v(2047.14, -3077.57) * mm});
            skLineSegment(sketch, "E154.9.45.0", {"start": v(2180.51, -3047.24) * mm, "end": v(2076, -3119.38) * mm});
            skLineSegment(sketch, "E154.1.46.0", {"start": v(2325.2, -2938.33) * mm, "end": v(2294.35, -2897.97) * mm});
            skLineSegment(sketch, "E154.3.46.0", {"start": v(2294.35, -2897.97) * mm, "end": v(2193.43, -2975.08) * mm});
            skLineSegment(sketch, "E154.6.46.0", {"start": v(2224.28, -3015.44) * mm, "end": v(2193.43, -2975.08) * mm});
            skLineSegment(sketch, "E154.9.46.0", {"start": v(2325.2, -2938.33) * mm, "end": v(2224.28, -3015.44) * mm});
            skLineSegment(sketch, "E154.1.47.0", {"start": v(2464.44, -2822.56) * mm, "end": v(2431.68, -2783.73) * mm});
            skLineSegment(sketch, "E154.3.47.0", {"start": v(2431.68, -2783.73) * mm, "end": v(2334.6, -2865.63) * mm});
            skLineSegment(sketch, "E154.6.47.0", {"start": v(2367.37, -2904.46) * mm, "end": v(2334.6, -2865.63) * mm});
            skLineSegment(sketch, "E154.9.47.0", {"start": v(2464.44, -2822.56) * mm, "end": v(2367.37, -2904.46) * mm});
            skLineSegment(sketch, "E154.1.48.0", {"start": v(2597.92, -2700.2) * mm, "end": v(2563.33, -2663) * mm});
            skLineSegment(sketch, "E154.3.48.0", {"start": v(2563.33, -2663) * mm, "end": v(2470.33, -2749.49) * mm});
            skLineSegment(sketch, "E154.6.48.0", {"start": v(2504.93, -2786.69) * mm, "end": v(2470.33, -2749.49) * mm});
            skLineSegment(sketch, "E154.9.48.0", {"start": v(2597.92, -2700.2) * mm, "end": v(2504.93, -2786.69) * mm});
            skLineSegment(sketch, "E154.1.49.0", {"start": v(2725.35, -2571.53) * mm, "end": v(2689, -2536.05) * mm});
            skLineSegment(sketch, "E154.3.49.0", {"start": v(2689, -2536.05) * mm, "end": v(2600.28, -2626.93) * mm});
            skLineSegment(sketch, "E154.6.49.0", {"start": v(2636.64, -2662.41) * mm, "end": v(2600.28, -2626.93) * mm});
            skLineSegment(sketch, "E154.9.49.0", {"start": v(2725.35, -2571.53) * mm, "end": v(2636.64, -2662.41) * mm});
            skLineSegment(sketch, "E154.1.50.0", {"start": v(2846.4, -2436.86) * mm, "end": v(2808.38, -2403.17) * mm});
            skLineSegment(sketch, "E154.3.50.0", {"start": v(2808.38, -2403.17) * mm, "end": v(2724.16, -2498.23) * mm});
            skLineSegment(sketch, "E154.6.50.0", {"start": v(2762.19, -2531.92) * mm, "end": v(2724.16, -2498.23) * mm});
            skLineSegment(sketch, "E154.9.50.0", {"start": v(2846.4, -2436.86) * mm, "end": v(2762.19, -2531.92) * mm});
            skLineSegment(sketch, "E154.1.51.0", {"start": v(2960.81, -2296.5) * mm, "end": v(2921.2, -2264.68) * mm});
            skLineSegment(sketch, "E154.3.51.0", {"start": v(2921.2, -2264.68) * mm, "end": v(2841.68, -2363.7) * mm});
            skLineSegment(sketch, "E154.6.51.0", {"start": v(2881.29, -2395.51) * mm, "end": v(2841.68, -2363.7) * mm});
            skLineSegment(sketch, "E154.9.51.0", {"start": v(2960.81, -2296.5) * mm, "end": v(2881.29, -2395.51) * mm});
            skLineSegment(sketch, "E154.1.52.0", {"start": v(3068.3, -2150.76) * mm, "end": v(3027.2, -2120.9) * mm});
            skLineSegment(sketch, "E154.3.52.0", {"start": v(3027.2, -2120.9) * mm, "end": v(2952.56, -2223.65) * mm});
            skLineSegment(sketch, "E154.6.52.0", {"start": v(2993.66, -2253.51) * mm, "end": v(2952.56, -2223.65) * mm});
            skLineSegment(sketch, "E154.9.52.0", {"start": v(3068.3, -2150.76) * mm, "end": v(2993.66, -2253.51) * mm});
            skLineSegment(sketch, "E154.1.53.0", {"start": v(3168.63, -2000.01) * mm, "end": v(3126.14, -1972.17) * mm});
            skLineSegment(sketch, "E154.3.53.0", {"start": v(3126.14, -1972.17) * mm, "end": v(3056.54, -2078.4) * mm});
            skLineSegment(sketch, "E154.6.53.0", {"start": v(3099.04, -2106.24) * mm, "end": v(3056.54, -2078.4) * mm});
            skLineSegment(sketch, "E154.9.53.0", {"start": v(3168.63, -2000.01) * mm, "end": v(3099.04, -2106.24) * mm});
            skLineSegment(sketch, "E154.1.54.0", {"start": v(3261.56, -1844.6) * mm, "end": v(3217.77, -1818.84) * mm});
            skLineSegment(sketch, "E154.3.54.0", {"start": v(3217.77, -1818.84) * mm, "end": v(3153.39, -1928.3) * mm});
            skLineSegment(sketch, "E154.6.54.0", {"start": v(3197.18, -1954.06) * mm, "end": v(3153.39, -1928.3) * mm});
            skLineSegment(sketch, "E154.9.54.0", {"start": v(3261.56, -1844.6) * mm, "end": v(3197.18, -1954.06) * mm});
            skLineSegment(sketch, "E154.1.55.0", {"start": v(3346.87, -1684.86) * mm, "end": v(3301.89, -1661.25) * mm});
            skLineSegment(sketch, "E154.3.55.0", {"start": v(3301.89, -1661.25) * mm, "end": v(3242.87, -1773.7) * mm});
            skLineSegment(sketch, "E154.6.55.0", {"start": v(3287.85, -1797.31) * mm, "end": v(3242.87, -1773.7) * mm});
            skLineSegment(sketch, "E154.9.55.0", {"start": v(3346.87, -1684.86) * mm, "end": v(3287.85, -1797.31) * mm});
            skLineSegment(sketch, "E154.1.56.0", {"start": v(3424.36, -1521.2) * mm, "end": v(3378.3, -1499.79) * mm});
            skLineSegment(sketch, "E154.3.56.0", {"start": v(3378.3, -1499.79) * mm, "end": v(3324.78, -1614.96) * mm});
            skLineSegment(sketch, "E154.6.56.0", {"start": v(3370.85, -1636.37) * mm, "end": v(3324.78, -1614.96) * mm});
            skLineSegment(sketch, "E154.9.56.0", {"start": v(3424.36, -1521.2) * mm, "end": v(3370.85, -1636.37) * mm});
            skLineSegment(sketch, "E154.1.57.0", {"start": v(3493.86, -1353.97) * mm, "end": v(3446.8, -1334.82) * mm});
            skLineSegment(sketch, "E154.3.57.0", {"start": v(3446.8, -1334.82) * mm, "end": v(3398.92, -1452.44) * mm});
            skLineSegment(sketch, "E154.6.57.0", {"start": v(3445.97, -1471.6) * mm, "end": v(3398.92, -1452.44) * mm});
            skLineSegment(sketch, "E154.9.57.0", {"start": v(3493.86, -1353.97) * mm, "end": v(3445.97, -1471.6) * mm});
            skLineSegment(sketch, "E154.1.58.0", {"start": v(3555.2, -1183.6) * mm, "end": v(3507.27, -1166.73) * mm});
            skLineSegment(sketch, "E154.3.58.0", {"start": v(3507.27, -1166.73) * mm, "end": v(3465.12, -1286.53) * mm});
            skLineSegment(sketch, "E154.6.58.0", {"start": v(3513.04, -1303.4) * mm, "end": v(3465.12, -1286.53) * mm});
            skLineSegment(sketch, "E154.9.58.0", {"start": v(3555.2, -1183.6) * mm, "end": v(3513.04, -1303.4) * mm});
            skLineSegment(sketch, "E154.1.59.0", {"start": v(3608.23, -1010.45) * mm, "end": v(3559.55, -995.92) * mm});
            skLineSegment(sketch, "E154.3.59.0", {"start": v(3559.55, -995.92) * mm, "end": v(3523.23, -1117.62) * mm});
            skLineSegment(sketch, "E154.6.59.0", {"start": v(3571.91, -1132.14) * mm, "end": v(3523.23, -1117.62) * mm});
            skLineSegment(sketch, "E154.9.59.0", {"start": v(3608.23, -1010.45) * mm, "end": v(3571.91, -1132.14) * mm});
            skLineSegment(sketch, "E154.1.60.0", {"start": v(3652.83, -834.94) * mm, "end": v(3603.5, -822.78) * mm});
            skLineSegment(sketch, "E154.3.60.0", {"start": v(3603.5, -822.78) * mm, "end": v(3573.11, -946.1) * mm});
            skLineSegment(sketch, "E154.6.60.0", {"start": v(3622.44, -958.25) * mm, "end": v(3573.11, -946.1) * mm});
            skLineSegment(sketch, "E154.9.60.0", {"start": v(3652.83, -834.94) * mm, "end": v(3622.44, -958.25) * mm});
            skLineSegment(sketch, "E154.1.61.0", {"start": v(3688.9, -657.49) * mm, "end": v(3639.05, -647.73) * mm});
            skLineSegment(sketch, "E154.3.61.0", {"start": v(3639.05, -647.73) * mm, "end": v(3614.65, -772.36) * mm});
            skLineSegment(sketch, "E154.6.61.0", {"start": v(3664.5, -782.12) * mm, "end": v(3614.65, -772.36) * mm});
            skLineSegment(sketch, "E154.9.61.0", {"start": v(3688.9, -657.49) * mm, "end": v(3664.5, -782.12) * mm});
            skLineSegment(sketch, "E154.1.62.0", {"start": v(3716.36, -478.5) * mm, "end": v(3666.1, -471.15) * mm});
            skLineSegment(sketch, "E154.3.62.0", {"start": v(3666.1, -471.15) * mm, "end": v(3647.74, -596.82) * mm});
            skLineSegment(sketch, "E154.6.62.0", {"start": v(3698.01, -604.16) * mm, "end": v(3647.74, -596.82) * mm});
            skLineSegment(sketch, "E154.9.62.0", {"start": v(3716.36, -478.5) * mm, "end": v(3698.01, -604.16) * mm});
            skLineSegment(sketch, "E154.1.63.0", {"start": v(3735.14, -298.39) * mm, "end": v(3684.58, -293.48) * mm});
            skLineSegment(sketch, "E154.3.63.0", {"start": v(3684.58, -293.48) * mm, "end": v(3672.32, -419.9) * mm});
            skLineSegment(sketch, "E154.6.63.0", {"start": v(3722.88, -424.8) * mm, "end": v(3672.32, -419.9) * mm});
            skLineSegment(sketch, "E154.9.63.0", {"start": v(3735.14, -298.39) * mm, "end": v(3722.88, -424.8) * mm});
            skLineSegment(sketch, "E154.1.64.0", {"start": v(3745.2, -117.58) * mm, "end": v(3694.45, -115.13) * mm});
            skLineSegment(sketch, "E154.3.64.0", {"start": v(3694.45, -115.13) * mm, "end": v(3688.32, -241.98) * mm});
            skLineSegment(sketch, "E154.6.64.0", {"start": v(3739.06, -244.43) * mm, "end": v(3688.32, -241.98) * mm});
            skLineSegment(sketch, "E154.9.64.0", {"start": v(3745.2, -117.58) * mm, "end": v(3739.06, -244.43) * mm});
            skLineSegment(sketch, "E154.1.65.0", {"start": v(3746.5, 63.5) * mm, "end": v(3695.7, 63.5) * mm});
            skLineSegment(sketch, "E154.3.65.0", {"start": v(3695.7, 63.5) * mm, "end": v(3695.7, -63.5) * mm});
            skLineSegment(sketch, "E154.6.65.0", {"start": v(3746.5, -63.5) * mm, "end": v(3695.7, -63.5) * mm});
            skLineSegment(sketch, "E154.9.65.0", {"start": v(3746.5, 63.5) * mm, "end": v(3746.5, -63.5) * mm});
            skLineSegment(sketch, "E154.1.66.0", {"start": v(3739.06, 244.43) * mm, "end": v(3688.32, 241.98) * mm});
            skLineSegment(sketch, "E154.3.66.0", {"start": v(3688.32, 241.98) * mm, "end": v(3694.45, 115.13) * mm});
            skLineSegment(sketch, "E154.6.66.0", {"start": v(3745.2, 117.58) * mm, "end": v(3694.45, 115.13) * mm});
            skLineSegment(sketch, "E154.9.66.0", {"start": v(3739.06, 244.43) * mm, "end": v(3745.2, 117.58) * mm});
            skLineSegment(sketch, "E154.1.67.0", {"start": v(3722.88, 424.8) * mm, "end": v(3672.32, 419.9) * mm});
            skLineSegment(sketch, "E154.3.67.0", {"start": v(3672.32, 419.9) * mm, "end": v(3684.58, 293.48) * mm});
            skLineSegment(sketch, "E154.6.67.0", {"start": v(3735.14, 298.39) * mm, "end": v(3684.58, 293.48) * mm});
            skLineSegment(sketch, "E154.9.67.0", {"start": v(3722.88, 424.8) * mm, "end": v(3735.14, 298.39) * mm});
            skLineSegment(sketch, "E154.1.68.0", {"start": v(3698.01, 604.16) * mm, "end": v(3647.74, 596.82) * mm});
            skLineSegment(sketch, "E154.3.68.0", {"start": v(3647.74, 596.82) * mm, "end": v(3666.1, 471.15) * mm});
            skLineSegment(sketch, "E154.6.68.0", {"start": v(3716.36, 478.5) * mm, "end": v(3666.1, 471.15) * mm});
            skLineSegment(sketch, "E154.9.68.0", {"start": v(3698.01, 604.16) * mm, "end": v(3716.36, 478.5) * mm});
            skLineSegment(sketch, "E154.1.69.0", {"start": v(3664.5, 782.12) * mm, "end": v(3614.65, 772.36) * mm});
            skLineSegment(sketch, "E154.3.69.0", {"start": v(3614.65, 772.36) * mm, "end": v(3639.05, 647.73) * mm});
            skLineSegment(sketch, "E154.6.69.0", {"start": v(3688.9, 657.49) * mm, "end": v(3639.05, 647.73) * mm});
            skLineSegment(sketch, "E154.9.69.0", {"start": v(3664.5, 782.12) * mm, "end": v(3688.9, 657.49) * mm});
            skLineSegment(sketch, "E154.1.70.0", {"start": v(3622.44, 958.25) * mm, "end": v(3573.11, 946.1) * mm});
            skLineSegment(sketch, "E154.3.70.0", {"start": v(3573.11, 946.1) * mm, "end": v(3603.5, 822.78) * mm});
            skLineSegment(sketch, "E154.6.70.0", {"start": v(3652.83, 834.94) * mm, "end": v(3603.5, 822.78) * mm});
            skLineSegment(sketch, "E154.9.70.0", {"start": v(3622.44, 958.25) * mm, "end": v(3652.83, 834.94) * mm});
            skLineSegment(sketch, "E154.1.71.0", {"start": v(3571.91, 1132.14) * mm, "end": v(3523.23, 1117.62) * mm});
            skLineSegment(sketch, "E154.3.71.0", {"start": v(3523.23, 1117.62) * mm, "end": v(3559.55, 995.92) * mm});
            skLineSegment(sketch, "E154.6.71.0", {"start": v(3608.23, 1010.45) * mm, "end": v(3559.55, 995.92) * mm});
            skLineSegment(sketch, "E154.9.71.0", {"start": v(3571.91, 1132.14) * mm, "end": v(3608.23, 1010.45) * mm});
            skLineSegment(sketch, "E154.1.72.0", {"start": v(3513.04, 1303.4) * mm, "end": v(3465.12, 1286.53) * mm});
            skLineSegment(sketch, "E154.3.72.0", {"start": v(3465.12, 1286.53) * mm, "end": v(3507.27, 1166.73) * mm});
            skLineSegment(sketch, "E154.6.72.0", {"start": v(3555.2, 1183.6) * mm, "end": v(3507.27, 1166.73) * mm});
            skLineSegment(sketch, "E154.9.72.0", {"start": v(3513.04, 1303.4) * mm, "end": v(3555.2, 1183.6) * mm});
            skLineSegment(sketch, "E154.1.73.0", {"start": v(3445.97, 1471.6) * mm, "end": v(3398.92, 1452.44) * mm});
            skLineSegment(sketch, "E154.3.73.0", {"start": v(3398.92, 1452.44) * mm, "end": v(3446.8, 1334.82) * mm});
            skLineSegment(sketch, "E154.6.73.0", {"start": v(3493.86, 1353.97) * mm, "end": v(3446.8, 1334.82) * mm});
            skLineSegment(sketch, "E154.9.73.0", {"start": v(3445.97, 1471.6) * mm, "end": v(3493.86, 1353.97) * mm});
            skLineSegment(sketch, "E154.1.74.0", {"start": v(3370.85, 1636.37) * mm, "end": v(3324.78, 1614.96) * mm});
            skLineSegment(sketch, "E154.3.74.0", {"start": v(3324.78, 1614.96) * mm, "end": v(3378.3, 1499.79) * mm});
            skLineSegment(sketch, "E154.6.74.0", {"start": v(3424.36, 1521.2) * mm, "end": v(3378.3, 1499.79) * mm});
            skLineSegment(sketch, "E154.9.74.0", {"start": v(3370.85, 1636.37) * mm, "end": v(3424.36, 1521.2) * mm});
            skLineSegment(sketch, "E154.1.75.0", {"start": v(3287.85, 1797.31) * mm, "end": v(3242.87, 1773.7) * mm});
            skLineSegment(sketch, "E154.3.75.0", {"start": v(3242.87, 1773.7) * mm, "end": v(3301.89, 1661.25) * mm});
            skLineSegment(sketch, "E154.6.75.0", {"start": v(3346.87, 1684.86) * mm, "end": v(3301.89, 1661.25) * mm});
            skLineSegment(sketch, "E154.9.75.0", {"start": v(3287.85, 1797.31) * mm, "end": v(3346.87, 1684.86) * mm});
            skLineSegment(sketch, "E154.1.76.0", {"start": v(3197.18, 1954.06) * mm, "end": v(3153.39, 1928.3) * mm});
            skLineSegment(sketch, "E154.3.76.0", {"start": v(3153.39, 1928.3) * mm, "end": v(3217.77, 1818.84) * mm});
            skLineSegment(sketch, "E154.6.76.0", {"start": v(3261.56, 1844.6) * mm, "end": v(3217.77, 1818.84) * mm});
            skLineSegment(sketch, "E154.9.76.0", {"start": v(3197.18, 1954.06) * mm, "end": v(3261.56, 1844.6) * mm});
            skLineSegment(sketch, "E154.1.77.0", {"start": v(3099.04, 2106.24) * mm, "end": v(3056.54, 2078.4) * mm});
            skLineSegment(sketch, "E154.3.77.0", {"start": v(3056.54, 2078.4) * mm, "end": v(3126.14, 1972.17) * mm});
            skLineSegment(sketch, "E154.6.77.0", {"start": v(3168.63, 2000.01) * mm, "end": v(3126.14, 1972.17) * mm});
            skLineSegment(sketch, "E154.9.77.0", {"start": v(3099.04, 2106.24) * mm, "end": v(3168.63, 2000.01) * mm});
            skLineSegment(sketch, "E154.1.78.0", {"start": v(2993.66, 2253.51) * mm, "end": v(2952.56, 2223.65) * mm});
            skLineSegment(sketch, "E154.3.78.0", {"start": v(2952.56, 2223.65) * mm, "end": v(3027.2, 2120.9) * mm});
            skLineSegment(sketch, "E154.6.78.0", {"start": v(3068.3, 2150.76) * mm, "end": v(3027.2, 2120.9) * mm});
            skLineSegment(sketch, "E154.9.78.0", {"start": v(2993.66, 2253.51) * mm, "end": v(3068.3, 2150.76) * mm});
            skLineSegment(sketch, "E154.1.79.0", {"start": v(2881.29, 2395.51) * mm, "end": v(2841.68, 2363.7) * mm});
            skLineSegment(sketch, "E154.3.79.0", {"start": v(2841.68, 2363.7) * mm, "end": v(2921.2, 2264.68) * mm});
            skLineSegment(sketch, "E154.6.79.0", {"start": v(2960.81, 2296.5) * mm, "end": v(2921.2, 2264.68) * mm});
            skLineSegment(sketch, "E154.9.79.0", {"start": v(2881.29, 2395.51) * mm, "end": v(2960.81, 2296.5) * mm});
            skLineSegment(sketch, "E154.1.80.0", {"start": v(2762.19, 2531.92) * mm, "end": v(2724.16, 2498.23) * mm});
            skLineSegment(sketch, "E154.3.80.0", {"start": v(2724.16, 2498.23) * mm, "end": v(2808.38, 2403.17) * mm});
            skLineSegment(sketch, "E154.6.80.0", {"start": v(2846.4, 2436.86) * mm, "end": v(2808.38, 2403.17) * mm});
            skLineSegment(sketch, "E154.9.80.0", {"start": v(2762.19, 2531.92) * mm, "end": v(2846.4, 2436.86) * mm});
            skLineSegment(sketch, "E154.1.81.0", {"start": v(2636.64, 2662.41) * mm, "end": v(2600.28, 2626.93) * mm});
            skLineSegment(sketch, "E154.3.81.0", {"start": v(2600.28, 2626.93) * mm, "end": v(2689, 2536.05) * mm});
            skLineSegment(sketch, "E154.6.81.0", {"start": v(2725.35, 2571.53) * mm, "end": v(2689, 2536.05) * mm});
            skLineSegment(sketch, "E154.9.81.0", {"start": v(2636.64, 2662.41) * mm, "end": v(2725.35, 2571.53) * mm});
            skLineSegment(sketch, "E154.1.82.0", {"start": v(2504.93, 2786.69) * mm, "end": v(2470.33, 2749.49) * mm});
            skLineSegment(sketch, "E154.3.82.0", {"start": v(2470.33, 2749.49) * mm, "end": v(2563.33, 2663) * mm});
            skLineSegment(sketch, "E154.6.82.0", {"start": v(2597.92, 2700.2) * mm, "end": v(2563.33, 2663) * mm});
            skLineSegment(sketch, "E154.9.82.0", {"start": v(2504.93, 2786.69) * mm, "end": v(2597.92, 2700.2) * mm});
            skLineSegment(sketch, "E154.1.83.0", {"start": v(2367.37, 2904.46) * mm, "end": v(2334.6, 2865.63) * mm});
            skLineSegment(sketch, "E154.3.83.0", {"start": v(2334.6, 2865.63) * mm, "end": v(2431.68, 2783.73) * mm});
            skLineSegment(sketch, "E154.6.83.0", {"start": v(2464.44, 2822.56) * mm, "end": v(2431.68, 2783.73) * mm});
            skLineSegment(sketch, "E154.9.83.0", {"start": v(2367.37, 2904.46) * mm, "end": v(2464.44, 2822.56) * mm});
            skLineSegment(sketch, "E154.1.84.0", {"start": v(2224.28, 3015.44) * mm, "end": v(2193.43, 2975.08) * mm});
            skLineSegment(sketch, "E154.3.84.0", {"start": v(2193.43, 2975.08) * mm, "end": v(2294.35, 2897.97) * mm});
            skLineSegment(sketch, "E154.6.84.0", {"start": v(2325.2, 2938.33) * mm, "end": v(2294.35, 2897.97) * mm});
            skLineSegment(sketch, "E154.9.84.0", {"start": v(2224.28, 3015.44) * mm, "end": v(2325.2, 2938.33) * mm});
            skLineSegment(sketch, "E154.1.85.0", {"start": v(2076, 3119.38) * mm, "end": v(2047.14, 3077.57) * mm});
            skLineSegment(sketch, "E154.3.85.0", {"start": v(2047.14, 3077.57) * mm, "end": v(2151.66, 3005.43) * mm});
            skLineSegment(sketch, "E154.6.85.0", {"start": v(2180.51, 3047.24) * mm, "end": v(2151.66, 3005.43) * mm});
            skLineSegment(sketch, "E154.9.85.0", {"start": v(2076, 3119.38) * mm, "end": v(2180.51, 3047.24) * mm});
            skLineSegment(sketch, "E154.1.86.0", {"start": v(1922.86, 3216.04) * mm, "end": v(1896.06, 3172.88) * mm});
            skLineSegment(sketch, "E154.3.86.0", {"start": v(1896.06, 3172.88) * mm, "end": v(2003.94, 3105.87) * mm});
            skLineSegment(sketch, "E154.6.86.0", {"start": v(2030.75, 3149.03) * mm, "end": v(2003.94, 3105.87) * mm});
            skLineSegment(sketch, "E154.9.86.0", {"start": v(1922.86, 3216.04) * mm, "end": v(2030.75, 3149.03) * mm});
            skLineSegment(sketch, "E154.1.87.0", {"start": v(1765.24, 3305.18) * mm, "end": v(1740.55, 3260.78) * mm});
            skLineSegment(sketch, "E154.3.87.0", {"start": v(1740.55, 3260.78) * mm, "end": v(1851.55, 3199.06) * mm});
            skLineSegment(sketch, "E154.6.87.0", {"start": v(1876.23, 3243.46) * mm, "end": v(1851.55, 3199.06) * mm});
            skLineSegment(sketch, "E154.9.87.0", {"start": v(1765.24, 3305.18) * mm, "end": v(1876.23, 3243.46) * mm});
            skLineSegment(sketch, "E154.1.88.0", {"start": v(1603.5, 3386.6) * mm, "end": v(1580.98, 3341.07) * mm});
            skLineSegment(sketch, "E154.3.88.0", {"start": v(1580.98, 3341.07) * mm, "end": v(1694.83, 3284.78) * mm});
            skLineSegment(sketch, "E154.6.88.0", {"start": v(1717.34, 3330.32) * mm, "end": v(1694.83, 3284.78) * mm});
            skLineSegment(sketch, "E154.9.88.0", {"start": v(1603.5, 3386.6) * mm, "end": v(1717.34, 3330.32) * mm});
            skLineSegment(sketch, "E154.1.89.0", {"start": v(1438, 3460.12) * mm, "end": v(1417.72, 3413.55) * mm});
            skLineSegment(sketch, "E154.3.89.0", {"start": v(1417.72, 3413.55) * mm, "end": v(1534.15, 3362.83) * mm});
            skLineSegment(sketch, "E154.6.89.0", {"start": v(1554.44, 3409.4) * mm, "end": v(1534.15, 3362.83) * mm});
            skLineSegment(sketch, "E154.9.89.0", {"start": v(1438, 3460.12) * mm, "end": v(1554.44, 3409.4) * mm});
            skLineSegment(sketch, "E154.1.90.0", {"start": v(1269.15, 3525.56) * mm, "end": v(1251.14, 3478.06) * mm});
            skLineSegment(sketch, "E154.3.90.0", {"start": v(1251.14, 3478.06) * mm, "end": v(1369.89, 3433.02) * mm});
            skLineSegment(sketch, "E154.6.90.0", {"start": v(1387.9, 3480.52) * mm, "end": v(1369.89, 3433.02) * mm});
            skLineSegment(sketch, "E154.9.90.0", {"start": v(1269.15, 3525.56) * mm, "end": v(1387.9, 3480.52) * mm});
            skLineSegment(sketch, "E154.1.91.0", {"start": v(1097.34, 3582.76) * mm, "end": v(1081.64, 3534.44) * mm});
            skLineSegment(sketch, "E154.3.91.0", {"start": v(1081.64, 3534.44) * mm, "end": v(1202.43, 3495.2) * mm});
            skLineSegment(sketch, "E154.6.91.0", {"start": v(1218.12, 3543.51) * mm, "end": v(1202.43, 3495.2) * mm});
            skLineSegment(sketch, "E154.9.91.0", {"start": v(1097.34, 3582.76) * mm, "end": v(1218.12, 3543.51) * mm});
            skLineSegment(sketch, "E154.1.92.0", {"start": v(922.96, 3631.59) * mm, "end": v(909.62, 3582.57) * mm});
            skLineSegment(sketch, "E154.3.92.0", {"start": v(909.62, 3582.57) * mm, "end": v(1032.16, 3549.2) * mm});
            skLineSegment(sketch, "E154.6.92.0", {"start": v(1045.5, 3598.22) * mm, "end": v(1032.16, 3549.2) * mm});
            skLineSegment(sketch, "E154.9.92.0", {"start": v(922.96, 3631.59) * mm, "end": v(1045.5, 3598.22) * mm});
            skLineSegment(sketch, "E154.1.93.0", {"start": v(746.43, 3671.94) * mm, "end": v(735.47, 3622.34) * mm});
            skLineSegment(sketch, "E154.3.93.0", {"start": v(735.47, 3622.34) * mm, "end": v(859.48, 3594.93) * mm});
            skLineSegment(sketch, "E154.6.93.0", {"start": v(870.44, 3644.53) * mm, "end": v(859.48, 3594.93) * mm});
            skLineSegment(sketch, "E154.9.93.0", {"start": v(746.43, 3671.94) * mm, "end": v(870.44, 3644.53) * mm});
            skLineSegment(sketch, "E154.1.94.0", {"start": v(568.16, 3703.71) * mm, "end": v(559.6, 3653.64) * mm});
            skLineSegment(sketch, "E154.3.94.0", {"start": v(559.6, 3653.64) * mm, "end": v(684.8, 3632.26) * mm});
            skLineSegment(sketch, "E154.6.94.0", {"start": v(693.34, 3682.33) * mm, "end": v(684.8, 3632.26) * mm});
            skLineSegment(sketch, "E154.9.94.0", {"start": v(568.16, 3703.71) * mm, "end": v(693.34, 3682.33) * mm});
            skLineSegment(sketch, "E154.1.95.0", {"start": v(388.55, 3726.84) * mm, "end": v(382.43, 3676.4) * mm});
            skLineSegment(sketch, "E154.3.95.0", {"start": v(382.43, 3676.4) * mm, "end": v(508.5, 3661.1) * mm});
            skLineSegment(sketch, "E154.6.95.0", {"start": v(514.63, 3711.53) * mm, "end": v(508.5, 3661.1) * mm});
            skLineSegment(sketch, "E154.9.95.0", {"start": v(388.55, 3726.84) * mm, "end": v(514.63, 3711.53) * mm});
            skLineSegment(sketch, "E154.1.96.0", {"start": v(208.04, 3741.26) * mm, "end": v(204.36, 3690.6) * mm});
            skLineSegment(sketch, "E154.3.96.0", {"start": v(204.36, 3690.6) * mm, "end": v(331.03, 3681.4) * mm});
            skLineSegment(sketch, "E154.6.96.0", {"start": v(334.71, 3732.06) * mm, "end": v(331.03, 3681.4) * mm});
            skLineSegment(sketch, "E154.9.96.0", {"start": v(208.04, 3741.26) * mm, "end": v(334.71, 3732.06) * mm});
            skLineSegment(sketch, "E154.1.97.0", {"start": v(27.05, 3746.94) * mm, "end": v(25.82, 3696.16) * mm});
            skLineSegment(sketch, "E154.3.97.0", {"start": v(25.82, 3696.16) * mm, "end": v(152.78, 3693.09) * mm});
            skLineSegment(sketch, "E154.6.97.0", {"start": v(154.01, 3743.87) * mm, "end": v(152.78, 3693.09) * mm});
            skLineSegment(sketch, "E154.9.97.0", {"start": v(27.05, 3746.94) * mm, "end": v(154.01, 3743.87) * mm});
            skLineSegment(sketch, "E154.1.98.0", {"start": v(-154.01, 3743.87) * mm, "end": v(-152.78, 3693.09) * mm});
            skLineSegment(sketch, "E154.3.98.0", {"start": v(-152.78, 3693.09) * mm, "end": v(-25.82, 3696.16) * mm});
            skLineSegment(sketch, "E154.6.98.0", {"start": v(-27.05, 3746.94) * mm, "end": v(-25.82, 3696.16) * mm});
            skLineSegment(sketch, "E154.9.98.0", {"start": v(-154.01, 3743.87) * mm, "end": v(-27.05, 3746.94) * mm});
            skLineSegment(sketch, "E154.1.99.0", {"start": v(-334.71, 3732.06) * mm, "end": v(-331.03, 3681.4) * mm});
            skLineSegment(sketch, "E154.3.99.0", {"start": v(-331.03, 3681.4) * mm, "end": v(-204.36, 3690.6) * mm});
            skLineSegment(sketch, "E154.6.99.0", {"start": v(-208.04, 3741.26) * mm, "end": v(-204.36, 3690.6) * mm});
            skLineSegment(sketch, "E154.9.99.0", {"start": v(-334.71, 3732.06) * mm, "end": v(-208.04, 3741.26) * mm});
            skLineSegment(sketch, "E154.1.100.0", {"start": v(-514.63, 3711.53) * mm, "end": v(-508.5, 3661.1) * mm});
            skLineSegment(sketch, "E154.3.100.0", {"start": v(-508.5, 3661.1) * mm, "end": v(-382.43, 3676.4) * mm});
            skLineSegment(sketch, "E154.6.100.0", {"start": v(-388.55, 3726.84) * mm, "end": v(-382.43, 3676.4) * mm});
            skLineSegment(sketch, "E154.9.100.0", {"start": v(-514.63, 3711.53) * mm, "end": v(-388.55, 3726.84) * mm});
            skLineSegment(sketch, "E154.1.101.0", {"start": v(-693.34, 3682.33) * mm, "end": v(-684.8, 3632.26) * mm});
            skLineSegment(sketch, "E154.3.101.0", {"start": v(-684.8, 3632.26) * mm, "end": v(-559.6, 3653.64) * mm});
            skLineSegment(sketch, "E154.6.101.0", {"start": v(-568.16, 3703.71) * mm, "end": v(-559.6, 3653.64) * mm});
            skLineSegment(sketch, "E154.9.101.0", {"start": v(-693.34, 3682.33) * mm, "end": v(-568.16, 3703.71) * mm});
            skLineSegment(sketch, "E154.1.102.0", {"start": v(-870.44, 3644.53) * mm, "end": v(-859.48, 3594.93) * mm});
            skLineSegment(sketch, "E154.3.102.0", {"start": v(-859.48, 3594.93) * mm, "end": v(-735.47, 3622.34) * mm});
            skLineSegment(sketch, "E154.6.102.0", {"start": v(-746.43, 3671.94) * mm, "end": v(-735.47, 3622.34) * mm});
            skLineSegment(sketch, "E154.9.102.0", {"start": v(-870.44, 3644.53) * mm, "end": v(-746.43, 3671.94) * mm});
            skLineSegment(sketch, "E154.1.103.0", {"start": v(-1045.5, 3598.22) * mm, "end": v(-1032.16, 3549.2) * mm});
            skLineSegment(sketch, "E154.3.103.0", {"start": v(-1032.16, 3549.2) * mm, "end": v(-909.62, 3582.57) * mm});
            skLineSegment(sketch, "E154.6.103.0", {"start": v(-922.96, 3631.59) * mm, "end": v(-909.62, 3582.57) * mm});
            skLineSegment(sketch, "E154.9.103.0", {"start": v(-1045.5, 3598.22) * mm, "end": v(-922.96, 3631.59) * mm});
            skLineSegment(sketch, "E154.1.104.0", {"start": v(-1218.12, 3543.51) * mm, "end": v(-1202.43, 3495.2) * mm});
            skLineSegment(sketch, "E154.3.104.0", {"start": v(-1202.43, 3495.2) * mm, "end": v(-1081.64, 3534.44) * mm});
            skLineSegment(sketch, "E154.6.104.0", {"start": v(-1097.34, 3582.76) * mm, "end": v(-1081.64, 3534.44) * mm});
            skLineSegment(sketch, "E154.9.104.0", {"start": v(-1218.12, 3543.51) * mm, "end": v(-1097.34, 3582.76) * mm});
            skLineSegment(sketch, "E154.1.105.0", {"start": v(-1387.9, 3480.52) * mm, "end": v(-1369.89, 3433.02) * mm});
            skLineSegment(sketch, "E154.3.105.0", {"start": v(-1369.89, 3433.02) * mm, "end": v(-1251.14, 3478.06) * mm});
            skLineSegment(sketch, "E154.6.105.0", {"start": v(-1269.15, 3525.56) * mm, "end": v(-1251.14, 3478.06) * mm});
            skLineSegment(sketch, "E154.9.105.0", {"start": v(-1387.9, 3480.52) * mm, "end": v(-1269.15, 3525.56) * mm});
            skLineSegment(sketch, "E154.1.106.0", {"start": v(-1554.44, 3409.4) * mm, "end": v(-1534.15, 3362.83) * mm});
            skLineSegment(sketch, "E154.3.106.0", {"start": v(-1534.15, 3362.83) * mm, "end": v(-1417.72, 3413.55) * mm});
            skLineSegment(sketch, "E154.6.106.0", {"start": v(-1438, 3460.12) * mm, "end": v(-1417.72, 3413.55) * mm});
            skLineSegment(sketch, "E154.9.106.0", {"start": v(-1554.44, 3409.4) * mm, "end": v(-1438, 3460.12) * mm});
            skLineSegment(sketch, "E154.1.107.0", {"start": v(-1717.34, 3330.32) * mm, "end": v(-1694.83, 3284.78) * mm});
            skLineSegment(sketch, "E154.3.107.0", {"start": v(-1694.83, 3284.78) * mm, "end": v(-1580.98, 3341.07) * mm});
            skLineSegment(sketch, "E154.6.107.0", {"start": v(-1603.5, 3386.6) * mm, "end": v(-1580.98, 3341.07) * mm});
            skLineSegment(sketch, "E154.9.107.0", {"start": v(-1717.34, 3330.32) * mm, "end": v(-1603.5, 3386.6) * mm});
            skLineSegment(sketch, "E154.1.108.0", {"start": v(-1876.23, 3243.46) * mm, "end": v(-1851.55, 3199.06) * mm});
            skLineSegment(sketch, "E154.3.108.0", {"start": v(-1851.55, 3199.06) * mm, "end": v(-1740.55, 3260.78) * mm});
            skLineSegment(sketch, "E154.6.108.0", {"start": v(-1765.24, 3305.18) * mm, "end": v(-1740.55, 3260.78) * mm});
            skLineSegment(sketch, "E154.9.108.0", {"start": v(-1876.23, 3243.46) * mm, "end": v(-1765.24, 3305.18) * mm});
            skLineSegment(sketch, "E154.1.109.0", {"start": v(-2030.75, 3149.03) * mm, "end": v(-2003.94, 3105.87) * mm});
            skLineSegment(sketch, "E154.3.109.0", {"start": v(-2003.94, 3105.87) * mm, "end": v(-1896.06, 3172.88) * mm});
            skLineSegment(sketch, "E154.6.109.0", {"start": v(-1922.86, 3216.04) * mm, "end": v(-1896.06, 3172.88) * mm});
            skLineSegment(sketch, "E154.9.109.0", {"start": v(-2030.75, 3149.03) * mm, "end": v(-1922.86, 3216.04) * mm});
            skLineSegment(sketch, "E154.1.110.0", {"start": v(-2180.51, 3047.24) * mm, "end": v(-2151.66, 3005.43) * mm});
            skLineSegment(sketch, "E154.3.110.0", {"start": v(-2151.66, 3005.43) * mm, "end": v(-2047.14, 3077.57) * mm});
            skLineSegment(sketch, "E154.6.110.0", {"start": v(-2076, 3119.38) * mm, "end": v(-2047.14, 3077.57) * mm});
            skLineSegment(sketch, "E154.9.110.0", {"start": v(-2180.51, 3047.24) * mm, "end": v(-2076, 3119.38) * mm});
            skLineSegment(sketch, "E154.1.111.0", {"start": v(-2325.2, 2938.33) * mm, "end": v(-2294.35, 2897.97) * mm});
            skLineSegment(sketch, "E154.3.111.0", {"start": v(-2294.35, 2897.97) * mm, "end": v(-2193.43, 2975.08) * mm});
            skLineSegment(sketch, "E154.6.111.0", {"start": v(-2224.28, 3015.44) * mm, "end": v(-2193.43, 2975.08) * mm});
            skLineSegment(sketch, "E154.9.111.0", {"start": v(-2325.2, 2938.33) * mm, "end": v(-2224.28, 3015.44) * mm});
            skLineSegment(sketch, "E154.1.112.0", {"start": v(-2464.44, 2822.56) * mm, "end": v(-2431.68, 2783.73) * mm});
            skLineSegment(sketch, "E154.3.112.0", {"start": v(-2431.68, 2783.73) * mm, "end": v(-2334.6, 2865.63) * mm});
            skLineSegment(sketch, "E154.6.112.0", {"start": v(-2367.37, 2904.46) * mm, "end": v(-2334.6, 2865.63) * mm});
            skLineSegment(sketch, "E154.9.112.0", {"start": v(-2464.44, 2822.56) * mm, "end": v(-2367.37, 2904.46) * mm});
            skLineSegment(sketch, "E154.1.113.0", {"start": v(-2597.92, 2700.2) * mm, "end": v(-2563.33, 2663) * mm});
            skLineSegment(sketch, "E154.3.113.0", {"start": v(-2563.33, 2663) * mm, "end": v(-2470.33, 2749.49) * mm});
            skLineSegment(sketch, "E154.6.113.0", {"start": v(-2504.93, 2786.69) * mm, "end": v(-2470.33, 2749.49) * mm});
            skLineSegment(sketch, "E154.9.113.0", {"start": v(-2597.92, 2700.2) * mm, "end": v(-2504.93, 2786.69) * mm});
            skLineSegment(sketch, "E154.1.114.0", {"start": v(-2725.35, 2571.53) * mm, "end": v(-2689, 2536.05) * mm});
            skLineSegment(sketch, "E154.3.114.0", {"start": v(-2689, 2536.05) * mm, "end": v(-2600.28, 2626.93) * mm});
            skLineSegment(sketch, "E154.6.114.0", {"start": v(-2636.64, 2662.41) * mm, "end": v(-2600.28, 2626.93) * mm});
            skLineSegment(sketch, "E154.9.114.0", {"start": v(-2725.35, 2571.53) * mm, "end": v(-2636.64, 2662.41) * mm});
            skLineSegment(sketch, "E154.1.115.0", {"start": v(-2846.4, 2436.86) * mm, "end": v(-2808.38, 2403.17) * mm});
            skLineSegment(sketch, "E154.3.115.0", {"start": v(-2808.38, 2403.17) * mm, "end": v(-2724.16, 2498.23) * mm});
            skLineSegment(sketch, "E154.6.115.0", {"start": v(-2762.19, 2531.92) * mm, "end": v(-2724.16, 2498.23) * mm});
            skLineSegment(sketch, "E154.9.115.0", {"start": v(-2846.4, 2436.86) * mm, "end": v(-2762.19, 2531.92) * mm});
            skLineSegment(sketch, "E154.1.116.0", {"start": v(-2960.81, 2296.5) * mm, "end": v(-2921.2, 2264.68) * mm});
            skLineSegment(sketch, "E154.3.116.0", {"start": v(-2921.2, 2264.68) * mm, "end": v(-2841.68, 2363.7) * mm});
            skLineSegment(sketch, "E154.6.116.0", {"start": v(-2881.29, 2395.51) * mm, "end": v(-2841.68, 2363.7) * mm});
            skLineSegment(sketch, "E154.9.116.0", {"start": v(-2960.81, 2296.5) * mm, "end": v(-2881.29, 2395.51) * mm});
            skLineSegment(sketch, "E154.1.117.0", {"start": v(-3068.3, 2150.76) * mm, "end": v(-3027.2, 2120.9) * mm});
            skLineSegment(sketch, "E154.3.117.0", {"start": v(-3027.2, 2120.9) * mm, "end": v(-2952.56, 2223.65) * mm});
            skLineSegment(sketch, "E154.6.117.0", {"start": v(-2993.66, 2253.51) * mm, "end": v(-2952.56, 2223.65) * mm});
            skLineSegment(sketch, "E154.9.117.0", {"start": v(-3068.3, 2150.76) * mm, "end": v(-2993.66, 2253.51) * mm});
            skLineSegment(sketch, "E154.1.118.0", {"start": v(-3168.63, 2000.01) * mm, "end": v(-3126.14, 1972.17) * mm});
            skLineSegment(sketch, "E154.3.118.0", {"start": v(-3126.14, 1972.17) * mm, "end": v(-3056.54, 2078.4) * mm});
            skLineSegment(sketch, "E154.6.118.0", {"start": v(-3099.04, 2106.24) * mm, "end": v(-3056.54, 2078.4) * mm});
            skLineSegment(sketch, "E154.9.118.0", {"start": v(-3168.63, 2000.01) * mm, "end": v(-3099.04, 2106.24) * mm});
            skLineSegment(sketch, "E154.1.119.0", {"start": v(-3261.56, 1844.6) * mm, "end": v(-3217.77, 1818.84) * mm});
            skLineSegment(sketch, "E154.3.119.0", {"start": v(-3217.77, 1818.84) * mm, "end": v(-3153.39, 1928.3) * mm});
            skLineSegment(sketch, "E154.6.119.0", {"start": v(-3197.18, 1954.06) * mm, "end": v(-3153.39, 1928.3) * mm});
            skLineSegment(sketch, "E154.9.119.0", {"start": v(-3261.56, 1844.6) * mm, "end": v(-3197.18, 1954.06) * mm});
            skLineSegment(sketch, "E154.1.120.0", {"start": v(-3346.87, 1684.86) * mm, "end": v(-3301.89, 1661.25) * mm});
            skLineSegment(sketch, "E154.3.120.0", {"start": v(-3301.89, 1661.25) * mm, "end": v(-3242.87, 1773.7) * mm});
            skLineSegment(sketch, "E154.6.120.0", {"start": v(-3287.85, 1797.31) * mm, "end": v(-3242.87, 1773.7) * mm});
            skLineSegment(sketch, "E154.9.120.0", {"start": v(-3346.87, 1684.86) * mm, "end": v(-3287.85, 1797.31) * mm});
            skLineSegment(sketch, "E154.1.121.0", {"start": v(-3424.36, 1521.2) * mm, "end": v(-3378.3, 1499.79) * mm});
            skLineSegment(sketch, "E154.3.121.0", {"start": v(-3378.3, 1499.79) * mm, "end": v(-3324.78, 1614.96) * mm});
            skLineSegment(sketch, "E154.6.121.0", {"start": v(-3370.85, 1636.37) * mm, "end": v(-3324.78, 1614.96) * mm});
            skLineSegment(sketch, "E154.9.121.0", {"start": v(-3424.36, 1521.2) * mm, "end": v(-3370.85, 1636.37) * mm});
            skLineSegment(sketch, "E154.1.122.0", {"start": v(-3493.86, 1353.97) * mm, "end": v(-3446.8, 1334.82) * mm});
            skLineSegment(sketch, "E154.3.122.0", {"start": v(-3446.8, 1334.82) * mm, "end": v(-3398.92, 1452.44) * mm});
            skLineSegment(sketch, "E154.6.122.0", {"start": v(-3445.97, 1471.6) * mm, "end": v(-3398.92, 1452.44) * mm});
            skLineSegment(sketch, "E154.9.122.0", {"start": v(-3493.86, 1353.97) * mm, "end": v(-3445.97, 1471.6) * mm});
            skLineSegment(sketch, "E154.1.123.0", {"start": v(-3555.2, 1183.6) * mm, "end": v(-3507.27, 1166.73) * mm});
            skLineSegment(sketch, "E154.3.123.0", {"start": v(-3507.27, 1166.73) * mm, "end": v(-3465.12, 1286.53) * mm});
            skLineSegment(sketch, "E154.6.123.0", {"start": v(-3513.04, 1303.4) * mm, "end": v(-3465.12, 1286.53) * mm});
            skLineSegment(sketch, "E154.9.123.0", {"start": v(-3555.2, 1183.6) * mm, "end": v(-3513.04, 1303.4) * mm});
            skLineSegment(sketch, "E154.1.124.0", {"start": v(-3608.23, 1010.45) * mm, "end": v(-3559.55, 995.92) * mm});
            skLineSegment(sketch, "E154.3.124.0", {"start": v(-3559.55, 995.92) * mm, "end": v(-3523.23, 1117.62) * mm});
            skLineSegment(sketch, "E154.6.124.0", {"start": v(-3571.91, 1132.14) * mm, "end": v(-3523.23, 1117.62) * mm});
            skLineSegment(sketch, "E154.9.124.0", {"start": v(-3608.23, 1010.45) * mm, "end": v(-3571.91, 1132.14) * mm});
            skLineSegment(sketch, "E154.1.125.0", {"start": v(-3652.83, 834.94) * mm, "end": v(-3603.5, 822.78) * mm});
            skLineSegment(sketch, "E154.3.125.0", {"start": v(-3603.5, 822.78) * mm, "end": v(-3573.11, 946.1) * mm});
            skLineSegment(sketch, "E154.6.125.0", {"start": v(-3622.44, 958.25) * mm, "end": v(-3573.11, 946.1) * mm});
            skLineSegment(sketch, "E154.9.125.0", {"start": v(-3652.83, 834.94) * mm, "end": v(-3622.44, 958.25) * mm});
            skLineSegment(sketch, "E154.1.126.0", {"start": v(-3688.9, 657.49) * mm, "end": v(-3639.05, 647.73) * mm});
            skLineSegment(sketch, "E154.3.126.0", {"start": v(-3639.05, 647.73) * mm, "end": v(-3614.65, 772.36) * mm});
            skLineSegment(sketch, "E154.6.126.0", {"start": v(-3664.5, 782.12) * mm, "end": v(-3614.65, 772.36) * mm});
            skLineSegment(sketch, "E154.9.126.0", {"start": v(-3688.9, 657.49) * mm, "end": v(-3664.5, 782.12) * mm});
            skLineSegment(sketch, "E154.1.127.0", {"start": v(-3716.36, 478.5) * mm, "end": v(-3666.1, 471.15) * mm});
            skLineSegment(sketch, "E154.3.127.0", {"start": v(-3666.1, 471.15) * mm, "end": v(-3647.74, 596.82) * mm});
            skLineSegment(sketch, "E154.6.127.0", {"start": v(-3698.01, 604.16) * mm, "end": v(-3647.74, 596.82) * mm});
            skLineSegment(sketch, "E154.9.127.0", {"start": v(-3716.36, 478.5) * mm, "end": v(-3698.01, 604.16) * mm});
            skLineSegment(sketch, "E154.1.128.0", {"start": v(-3735.14, 298.39) * mm, "end": v(-3684.58, 293.48) * mm});
            skLineSegment(sketch, "E154.3.128.0", {"start": v(-3684.58, 293.48) * mm, "end": v(-3672.32, 419.9) * mm});
            skLineSegment(sketch, "E154.6.128.0", {"start": v(-3722.88, 424.8) * mm, "end": v(-3672.32, 419.9) * mm});
            skLineSegment(sketch, "E154.9.128.0", {"start": v(-3735.14, 298.39) * mm, "end": v(-3722.88, 424.8) * mm});
            skLineSegment(sketch, "E154.1.129.0", {"start": v(-3745.2, 117.58) * mm, "end": v(-3694.45, 115.13) * mm});
            skLineSegment(sketch, "E154.3.129.0", {"start": v(-3694.45, 115.13) * mm, "end": v(-3688.32, 241.98) * mm});
            skLineSegment(sketch, "E154.6.129.0", {"start": v(-3739.06, 244.43) * mm, "end": v(-3688.32, 241.98) * mm});
            skLineSegment(sketch, "E154.9.129.0", {"start": v(-3745.2, 117.58) * mm, "end": v(-3739.06, 244.43) * mm});
            skSolve(sketch);
        }
        {
            var Q0;
            Q0=makeQuery(id+"F0.imprint","IMPRINT",FACE,{"disambiguationData":[TD([[makeQuery(id+"F0.imprint","IMPRINT",EDGE,{"derivedFrom":sQuery(id+"F0.wireOp",EDGE,"E151.bottom")}),-1.0]])]});
            var Q1;
            {var subQ0=sQuery(id+"F0.wireOp",EDGE,"E153");var subQ1=sQuery(id+"F0.wireOp",EDGE,"E144");var subQ2=makeQuery(id+"F0.imprint","INTERSECT",VERTEX,{"derivedFrom":[subQ1,subQ0]});Q1=makeQuery(id+"F0.imprint","IMPRINT",FACE,{"disambiguationData":[TD([[makeQuery(id+"F0.imprint","IMPRINT",EDGE,{"disambiguationData":[TD([[subQ2,1.0]])],"derivedFrom":subQ1}),-1.0]])]});}
            var Q2;
            Q2=makeQuery(id+"F0.imprint","IMPRINT",FACE,{"disambiguationData":[TD([[makeQuery(id+"F0.imprint","IMPRINT",EDGE,{"derivedFrom":sQuery(id+"F0.wireOp",EDGE,"E148")}),-1.0]])]});
            var Q3;
            {var subQ0=sQuery(id+"F0.wireOp",EDGE,"E143");var subQ1=sQuery(id+"F0.wireOp",EDGE,"E119.bottom");var subQ2=makeQuery(id+"F0.imprint","INTERSECT",VERTEX,{"derivedFrom":[subQ1,subQ0]});Q3=makeQuery(id+"F0.imprint","IMPRINT",FACE,{"disambiguationData":[TD([[makeQuery(id+"F0.imprint","IMPRINT",EDGE,{"disambiguationData":[TD([[subQ2,-1.0]])],"derivedFrom":subQ1}),-1.0]])]});}
            var Q4;
            Q4=makeQuery(id+"F0.imprint","IMPRINT",FACE,{"disambiguationData":[TD([[makeQuery(id+"F0.imprint","IMPRINT",EDGE,{"derivedFrom":sQuery(id+"F0.wireOp",EDGE,"E102")}),-1.0]])]});
            extrude(context, id + "F1", {"entities" : qUnion([Q0, Q1, Q2, Q3, Q4]), "depth" : 76.2 * mm, "offsetDistance" : 25.4 * mm});
        }
        {
            var Q0;
            Q0=makeQuery(id+"F1.opExtrude","SWEPT_EDGE",EDGE,{"disambiguationData":[OSD([sQuery(id+"F0.wireOp",EDGE,"E144"),sQuery(id+"F0.wireOp",EDGE,"E153")])]});
            fillet(context, id + "F2", {"entities" : qUnion([Q0]), "radius" : 762 * mm, "tangentPropagation" : true, "defaultsChanged" : false, "vertexSettings" : [], "allowEdgeOverflow" : false});
        }
        {
            var Q0;
            Q0=makeQuery(id+"F1.opExtrude","SWEPT_EDGE",EDGE,{"disambiguationData":[OSD([sQuery(id+"FpJHvg5FOVo1zxj_0.wireOp",EDGE,"KnNI1HOa-Nymh-Zg6Q-qHNo-bmVBBbPtuTZB"),sQuery(id+"FpJHvg5FOVo1zxj_0.wireOp",EDGE,"byGwwOY5-X2k2-Kkgf-xbZV-TotlOvGy45os")])]});
            var Q1;
            Q1=makeQuery(id+"F1.opExtrude","SWEPT_EDGE",EDGE,{"disambiguationData":[OSD([sQuery(id+"FpJHvg5FOVo1zxj_0.wireOp",EDGE,"mz7DBWGo-IWmh-fLji-a27y-32KiiZUIhtLe.bottom"),sQuery(id+"FpJHvg5FOVo1zxj_0.wireOp",EDGE,"KnNI1HOa-Nymh-Zg6Q-qHNo-bmVBBbPtuTZB")])]});
            var Q2;
            Q2=makeQuery(id+"F2.opFillet","BLEND_EDGE",EDGE,{"blendedFrom":[makeQuery(id+"F1.opExtrude","SWEPT_EDGE",EDGE,{"disambiguationData":[OSD([sQuery(id+"F0.wireOp",EDGE,"E144"),sQuery(id+"F0.wireOp",EDGE,"E153")])]}),makeQuery(id+"F1.opExtrude","SWEPT_FACE",FACE,{"disambiguationData":[OSD([sQuery(id+"F0.wireOp",EDGE,"E150")])]})],"blendedInto":[makeQuery(id+"F1.opExtrude","SWEPT_FACE",FACE,{"disambiguationData":[OSD([sQuery(id+"F0.wireOp",EDGE,"E150")])]})]});
            var Q3;
            Q3=makeQuery(id+"F1.opExtrude","SWEPT_EDGE",EDGE,{"disambiguationData":[OSD([sQuery(id+"F0.wireOp",EDGE,"E149"),sQuery(id+"F0.wireOp",EDGE,"E150")])]});
            var Q4;
            Q4=makeQuery(id+"F1.opExtrude","SWEPT_EDGE",EDGE,{"disambiguationData":[OSD([sQuery(id+"F0.wireOp",EDGE,"E143"),sQuery(id+"F0.wireOp",EDGE,"E149")])]});
            var Q5;
            Q5=makeQuery(id+"F1.opExtrude","SWEPT_EDGE",EDGE,{"disambiguationData":[OSD([sQuery(id+"F0.wireOp",EDGE,"E119.top"),sQuery(id+"F0.wireOp",EDGE,"E143")])]});
            var Q6;
            Q6=makeQuery(id+"F1.opExtrude","SWEPT_EDGE",EDGE,{"disambiguationData":[OSD([sQuery(id+"F0.wireOp",EDGE,"E119.top"),sQuery(id+"F0.wireOp",EDGE,"E144")])]});
            fillet(context, id + "F3", {"entities" : qUnion([Q0, Q1, Q2, Q3, Q4, Q5, Q6]), "radius" : 63.5 * mm, "tangentPropagation" : true, "defaultsChanged" : false, "vertexSettings" : [], "allowEdgeOverflow" : false});
        }
    });
